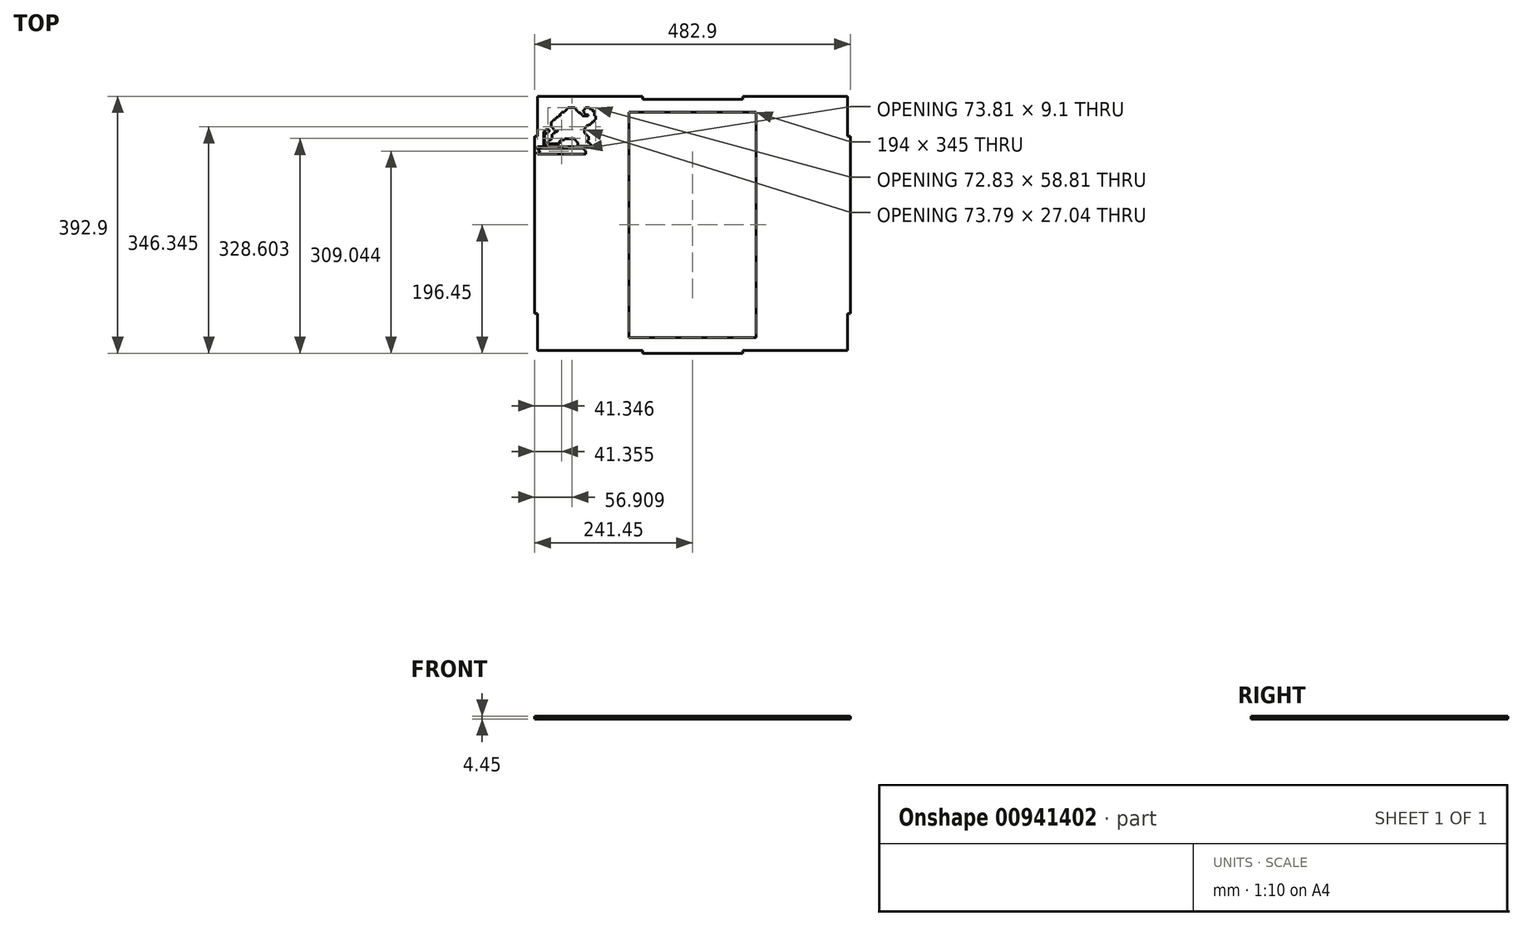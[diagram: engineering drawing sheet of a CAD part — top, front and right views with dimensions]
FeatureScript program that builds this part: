
annotation { "Feature Type Name" : "Feature", "Feature Type Description" : "" }
export const myFeature = defineFeature(function(context is Context, id is Id, definition is map)
    precondition{}
    {
        {
            var Q0;
            Q0=qCreatedBy(makeId("Top.planeOp"),FACE);
            var sketch = newSketch(context, id + "F0", { "sketchPlane" : qUnion([Q0])});
            skLineSegment(sketch, "E0.bottom", {"start": v(97, -172.5) * mm, "end": v(-97, -172.5) * mm});
            skLineSegment(sketch, "E0.top", {"start": v(97, 172.5) * mm, "end": v(-97, 172.5) * mm});
            skLineSegment(sketch, "E0.left", {"start": v(97, -172.5) * mm, "end": v(97, 172.5) * mm});
            skLineSegment(sketch, "E0.right", {"start": v(-97, -172.5) * mm, "end": v(-97, 172.5) * mm});
            skPoint(sketch, "E0.middle", {"position": v(0, 0) * mm});
            skLineSegment(sketch, "E1.bottom", {"start": v(237, -192) * mm, "end": v(76.58, -192) * mm});
            skLineSegment(sketch, "E1.top", {"start": v(76.58, 192) * mm, "end": v(-76.58, 192) * mm});
            skLineSegment(sketch, "E1.left", {"start": v(237, -192) * mm, "end": v(237, -135.76) * mm});
            skLineSegment(sketch, "E1.right", {"start": v(-237, -192) * mm, "end": v(-237, -135.76) * mm});
            skLineSegment(sketch, "E2.top", {"start": v(-237, 196.45) * mm, "end": v(-76.58, 196.45) * mm});
            skLineSegment(sketch, "E2.left", {"start": v(-237, 192) * mm, "end": v(-237, 196.45) * mm});
            skLineSegment(sketch, "E2.right", {"start": v(-76.58, 192) * mm, "end": v(-76.58, 196.45) * mm});
            skLineSegment(sketch, "E3.MirrorCS", {"start": v(76.58, 192) * mm, "end": v(76.58, 196.45) * mm});
            skLineSegment(sketch, "E4.MirrorCS", {"start": v(237, 196.45) * mm, "end": v(76.58, 196.45) * mm});
            skLineSegment(sketch, "E5.MirrorCS", {"start": v(237, 192) * mm, "end": v(237, 196.45) * mm});
            skLineSegment(sketch, "E6.top", {"start": v(-76.58, -196.45) * mm, "end": v(76.58, -196.45) * mm});
            skLineSegment(sketch, "E6.left", {"start": v(-76.58, -192) * mm, "end": v(-76.58, -196.45) * mm});
            skLineSegment(sketch, "E6.right", {"start": v(76.58, -192) * mm, "end": v(76.58, -196.45) * mm});
            skLineSegment(sketch, "E7.trimOffspring", {"start": v(-76.58, -192) * mm, "end": v(-237, -192) * mm});
            skLineSegment(sketch, "E8.bottom", {"start": v(241.45, -135.76) * mm, "end": v(237, -135.76) * mm});
            skLineSegment(sketch, "E8.top", {"start": v(241.45, 135.76) * mm, "end": v(237, 135.76) * mm});
            skLineSegment(sketch, "E8.left", {"start": v(241.45, -135.76) * mm, "end": v(241.45, 135.76) * mm});
            skLineSegment(sketch, "E8.right", {"start": v(-241.45, -135.76) * mm, "end": v(-241.45, 135.76) * mm});
            skLineSegment(sketch, "E9.trimOffspring", {"start": v(-237, 135.76) * mm, "end": v(-241.45, 135.76) * mm});
            skLineSegment(sketch, "E10.trimOffspring", {"start": v(-237, -135.76) * mm, "end": v(-241.45, -135.76) * mm});
            skLineSegment(sketch, "E11.trimOffspring", {"start": v(-237, 135.76) * mm, "end": v(-237, 192) * mm});
            skLineSegment(sketch, "E12.trimOffspring", {"start": v(237, 135.76) * mm, "end": v(237, 192) * mm});
            skLineSegment(sketch, "E13", {"start": v(-234.26, 117.12) * mm, "end": v(-234.26, 115.6) * mm});
            skLineSegment(sketch, "E14", {"start": v(-234.26, 115.6) * mm, "end": v(-232.83, 115.6) * mm});
            skLineSegment(sketch, "E15", {"start": v(-232.83, 115.6) * mm, "end": v(-232.83, 114.12) * mm});
            skLineSegment(sketch, "E16", {"start": v(-232.83, 114.12) * mm, "end": v(-231.4, 114.12) * mm});
            skLineSegment(sketch, "E17", {"start": v(-231.4, 114.12) * mm, "end": v(-231.4, 112.74) * mm});
            skLineSegment(sketch, "E18", {"start": v(-231.4, 112.74) * mm, "end": v(-230.13, 112.74) * mm});
            skLineSegment(sketch, "E19", {"start": v(-230.13, 112.74) * mm, "end": v(-230.13, 114.17) * mm});
            skLineSegment(sketch, "E20", {"start": v(-230.13, 114.17) * mm, "end": v(-228.66, 114.17) * mm});
            skLineSegment(sketch, "E21", {"start": v(-228.66, 114.17) * mm, "end": v(-228.66, 115.71) * mm});
            skLineSegment(sketch, "E22", {"start": v(-228.66, 115.71) * mm, "end": v(-227.2, 115.71) * mm});
            skLineSegment(sketch, "E23", {"start": v(-227.2, 115.71) * mm, "end": v(-227.2, 117.12) * mm});
            skLineSegment(sketch, "E24", {"start": v(-227.2, 117.12) * mm, "end": v(-222.93, 117.12) * mm});
            skLineSegment(sketch, "E25", {"start": v(-222.93, 117.12) * mm, "end": v(-222.93, 115.71) * mm});
            skLineSegment(sketch, "E26", {"start": v(-222.93, 115.71) * mm, "end": v(-221.5, 115.71) * mm});
            skLineSegment(sketch, "E27", {"start": v(-221.5, 115.71) * mm, "end": v(-221.5, 114.06) * mm});
            skLineSegment(sketch, "E28", {"start": v(-221.5, 114.06) * mm, "end": v(-220.04, 114.06) * mm});
            skLineSegment(sketch, "E29", {"start": v(-220.04, 114.06) * mm, "end": v(-220.04, 112.71) * mm});
            skLineSegment(sketch, "E30", {"start": v(-220.04, 112.71) * mm, "end": v(-218.69, 112.71) * mm});
            skLineSegment(sketch, "E31", {"start": v(-218.69, 112.71) * mm, "end": v(-218.69, 114.06) * mm});
            skLineSegment(sketch, "E32", {"start": v(-218.69, 114.06) * mm, "end": v(-217.28, 114.06) * mm});
            skLineSegment(sketch, "E33", {"start": v(-217.28, 114.06) * mm, "end": v(-217.28, 115.58) * mm});
            skLineSegment(sketch, "E34", {"start": v(-217.28, 115.58) * mm, "end": v(-215.87, 115.58) * mm});
            skLineSegment(sketch, "E35", {"start": v(-215.87, 115.58) * mm, "end": v(-215.87, 117.15) * mm});
            skLineSegment(sketch, "E36", {"start": v(-215.87, 117.15) * mm, "end": v(-211.57, 117.15) * mm});
            skLineSegment(sketch, "E37", {"start": v(-211.57, 117.15) * mm, "end": v(-211.57, 115.69) * mm});
            skLineSegment(sketch, "E38", {"start": v(-211.57, 115.69) * mm, "end": v(-210.14, 115.69) * mm});
            skLineSegment(sketch, "E39", {"start": v(-210.14, 115.69) * mm, "end": v(-210.14, 114.06) * mm});
            skLineSegment(sketch, "E40", {"start": v(-210.14, 114.06) * mm, "end": v(-208.7, 114.06) * mm});
            skLineSegment(sketch, "E41", {"start": v(-208.7, 114.06) * mm, "end": v(-208.7, 112.71) * mm});
            skLineSegment(sketch, "E42", {"start": v(-208.7, 112.71) * mm, "end": v(-207.82, 112.71) * mm});
            skLineSegment(sketch, "E43", {"start": v(-207.82, 112.71) * mm, "end": v(-207.82, 114.06) * mm});
            skLineSegment(sketch, "E44", {"start": v(-207.82, 114.06) * mm, "end": v(-206.65, 114.06) * mm});
            skLineSegment(sketch, "E45", {"start": v(-206.65, 114.06) * mm, "end": v(-206.65, 115.58) * mm});
            skLineSegment(sketch, "E46", {"start": v(-206.65, 115.58) * mm, "end": v(-205.3, 115.58) * mm});
            skLineSegment(sketch, "E47", {"start": v(-205.3, 115.58) * mm, "end": v(-205.3, 117.1) * mm});
            skLineSegment(sketch, "E48", {"start": v(-234.26, 117.12) * mm, "end": v(-237, 117.12) * mm});
            skLineSegment(sketch, "E49", {"start": v(-237, 117.12) * mm, "end": v(-237, 115.63) * mm});
            skLineSegment(sketch, "E50", {"start": v(-237, 115.63) * mm, "end": v(-235.7, 115.63) * mm});
            skLineSegment(sketch, "E51", {"start": v(-235.7, 115.63) * mm, "end": v(-235.7, 114.12) * mm});
            skLineSegment(sketch, "E52", {"start": v(-235.7, 114.12) * mm, "end": v(-234.26, 114.12) * mm});
            skLineSegment(sketch, "E53", {"start": v(-234.26, 114.12) * mm, "end": v(-234.26, 112.6) * mm});
            skLineSegment(sketch, "E54", {"start": v(-234.26, 112.6) * mm, "end": v(-232.86, 112.6) * mm});
            skLineSegment(sketch, "E55", {"start": v(-232.86, 112.6) * mm, "end": v(-232.86, 111.09) * mm});
            skLineSegment(sketch, "E56", {"start": v(-232.86, 111.09) * mm, "end": v(-237, 111.09) * mm});
            skLineSegment(sketch, "E57", {"start": v(-237, 111.09) * mm, "end": v(-237, 109.63) * mm});
            skLineSegment(sketch, "E58", {"start": v(-237, 109.63) * mm, "end": v(-163.2, 109.63) * mm});
            skLineSegment(sketch, "E59", {"start": v(-163.2, 109.63) * mm, "end": v(-163.2, 112.67) * mm});
            skLineSegment(sketch, "E60", {"start": v(-163.2, 112.67) * mm, "end": v(-163.98, 112.67) * mm});
            skLineSegment(sketch, "E61", {"start": v(-163.98, 112.67) * mm, "end": v(-163.98, 114.08) * mm});
            skLineSegment(sketch, "E62", {"start": v(-163.98, 114.08) * mm, "end": v(-165.32, 114.08) * mm});
            skLineSegment(sketch, "E63", {"start": v(-165.32, 114.08) * mm, "end": v(-165.32, 115.6) * mm});
            skLineSegment(sketch, "E64", {"start": v(-165.32, 115.6) * mm, "end": v(-166.82, 115.6) * mm});
            skLineSegment(sketch, "E65", {"start": v(-166.82, 115.6) * mm, "end": v(-166.82, 117.12) * mm});
            skLineSegment(sketch, "E66", {"start": v(-166.82, 117.12) * mm, "end": v(-171.1, 117.12) * mm});
            skLineSegment(sketch, "E67", {"start": v(-171.1, 117.12) * mm, "end": v(-171.1, 115.6) * mm});
            skLineSegment(sketch, "E68", {"start": v(-171.1, 115.6) * mm, "end": v(-172.46, 115.6) * mm});
            skLineSegment(sketch, "E69", {"start": v(-172.46, 115.6) * mm, "end": v(-172.46, 114.06) * mm});
            skLineSegment(sketch, "E70", {"start": v(-172.46, 114.06) * mm, "end": v(-173.99, 114.06) * mm});
            skLineSegment(sketch, "E71", {"start": v(-173.99, 114.06) * mm, "end": v(-173.99, 112.67) * mm});
            skLineSegment(sketch, "E72.bottom", {"start": v(-205.3, 117.1) * mm, "end": v(-200.98, 117.1) * mm});
            skLineSegment(sketch, "E72.top", {"start": v(-203.8, 115.63) * mm, "end": v(-202.3, 115.63) * mm});
            skLineSegment(sketch, "E72.left", {"start": v(-205.3, 117.1) * mm, "end": v(-205.3, 115.63) * mm});
            skLineSegment(sketch, "E72.right", {"start": v(-200.98, 117.1) * mm, "end": v(-200.98, 115.63) * mm});
            skLineSegment(sketch, "E73.bottom", {"start": v(-200.98, 115.63) * mm, "end": v(-199.6, 115.63) * mm});
            skLineSegment(sketch, "E73.top", {"start": v(-202.3, 114.04) * mm, "end": v(-200.95, 114.04) * mm});
            skLineSegment(sketch, "E73.left", {"start": v(-202.3, 115.63) * mm, "end": v(-202.3, 114.04) * mm});
            skLineSegment(sketch, "E73.right", {"start": v(-199.6, 115.63) * mm, "end": v(-199.6, 114.04) * mm});
            skLineSegment(sketch, "E74.bottom", {"start": v(-199.6, 114.04) * mm, "end": v(-198.16, 114.04) * mm});
            skLineSegment(sketch, "E74.top", {"start": v(-200.95, 112.74) * mm, "end": v(-199.55, 112.74) * mm});
            skLineSegment(sketch, "E74.left", {"start": v(-200.95, 114.04) * mm, "end": v(-200.95, 112.74) * mm});
            skLineSegment(sketch, "E74.right", {"start": v(-198.16, 114.04) * mm, "end": v(-198.16, 112.74) * mm});
            skLineSegment(sketch, "E75.bottom", {"start": v(-198.16, 112.74) * mm, "end": v(-196.75, 112.74) * mm});
            skLineSegment(sketch, "E75.left", {"start": v(-199.55, 112.74) * mm, "end": v(-199.55, 111.08) * mm});
            skLineSegment(sketch, "E75.right", {"start": v(-195.3, 112.74) * mm, "end": v(-195.3, 111.08) * mm});
            skLineSegment(sketch, "E76.bottom", {"start": v(-196.75, 114.1) * mm, "end": v(-195.3, 114.1) * mm});
            skLineSegment(sketch, "E76.top", {"start": v(-195.3, 112.74) * mm, "end": v(-193.95, 112.74) * mm});
            skLineSegment(sketch, "E76.left", {"start": v(-196.75, 114.1) * mm, "end": v(-196.75, 112.74) * mm});
            skLineSegment(sketch, "E76.right", {"start": v(-193.95, 114.1) * mm, "end": v(-193.95, 112.74) * mm});
            skLineSegment(sketch, "E77.top", {"start": v(-193.95, 114.1) * mm, "end": v(-192.4, 114.1) * mm});
            skLineSegment(sketch, "E77.left", {"start": v(-195.3, 115.58) * mm, "end": v(-195.3, 114.1) * mm});
            skLineSegment(sketch, "E77.right", {"start": v(-192.4, 115.58) * mm, "end": v(-192.4, 114.1) * mm});
            skLineSegment(sketch, "E78.bottom", {"start": v(-193.94, 117.1) * mm, "end": v(-189.56, 117.1) * mm});
            skLineSegment(sketch, "E78.left", {"start": v(-193.94, 117.1) * mm, "end": v(-193.94, 115.58) * mm});
            skLineSegment(sketch, "E78.right", {"start": v(-189.56, 117.1) * mm, "end": v(-189.56, 115.58) * mm});
            skLineSegment(sketch, "E79", {"start": v(-203.8, 115.63) * mm, "end": v(-203.8, 114.15) * mm});
            skLineSegment(sketch, "E80", {"start": v(-203.8, 114.15) * mm, "end": v(-205.27, 114.15) * mm});
            skLineSegment(sketch, "E81", {"start": v(-205.27, 114.15) * mm, "end": v(-205.27, 112.63) * mm});
            skLineSegment(sketch, "E82", {"start": v(-205.27, 112.63) * mm, "end": v(-206.61, 112.63) * mm});
            skLineSegment(sketch, "E83", {"start": v(-206.61, 112.63) * mm, "end": v(-206.61, 111.15) * mm});
            skLineSegment(sketch, "E84", {"start": v(-206.61, 111.15) * mm, "end": v(-199.55, 111.08) * mm});
            skLineSegment(sketch, "E85.bottom", {"start": v(-189.56, 115.58) * mm, "end": v(-188.16, 115.58) * mm});
            skLineSegment(sketch, "E85.top", {"start": v(-191.02, 114.05) * mm, "end": v(-189.6, 114.05) * mm});
            skLineSegment(sketch, "E85.left", {"start": v(-191.02, 115.58) * mm, "end": v(-191.02, 114.05) * mm});
            skLineSegment(sketch, "E85.right", {"start": v(-188.16, 115.58) * mm, "end": v(-188.16, 114.05) * mm});
            skLineSegment(sketch, "E86.bottom", {"start": v(-188.16, 114.05) * mm, "end": v(-186.74, 114.05) * mm});
            skLineSegment(sketch, "E86.top", {"start": v(-189.6, 112.64) * mm, "end": v(-188.16, 112.64) * mm});
            skLineSegment(sketch, "E86.left", {"start": v(-189.6, 114.05) * mm, "end": v(-189.6, 112.64) * mm});
            skLineSegment(sketch, "E86.right", {"start": v(-186.74, 114.05) * mm, "end": v(-186.74, 112.64) * mm});
            skLineSegment(sketch, "E87.bottom", {"start": v(-186.74, 112.64) * mm, "end": v(-185.4, 112.64) * mm});
            skLineSegment(sketch, "E87.left", {"start": v(-188.16, 112.64) * mm, "end": v(-188.16, 111.08) * mm});
            skLineSegment(sketch, "E87.right", {"start": v(-183.94, 112.64) * mm, "end": v(-183.94, 111.08) * mm});
            skLineSegment(sketch, "E88", {"start": v(-195.3, 111.08) * mm, "end": v(-188.16, 111.08) * mm});
            skLineSegment(sketch, "E89", {"start": v(-183.94, 112.64) * mm, "end": v(-182.48, 112.64) * mm});
            skLineSegment(sketch, "E90", {"start": v(-182.48, 112.64) * mm, "end": v(-182.48, 114.04) * mm});
            skLineSegment(sketch, "E91", {"start": v(-182.48, 114.04) * mm, "end": v(-181.05, 114.04) * mm});
            skLineSegment(sketch, "E92", {"start": v(-181.05, 114.04) * mm, "end": v(-181.05, 115.56) * mm});
            skLineSegment(sketch, "E93", {"start": v(-181.05, 115.56) * mm, "end": v(-179.73, 115.56) * mm});
            skLineSegment(sketch, "E94", {"start": v(-179.73, 115.56) * mm, "end": v(-179.73, 114.04) * mm});
            skLineSegment(sketch, "E95", {"start": v(-179.73, 114.04) * mm, "end": v(-178.33, 114.04) * mm});
            skLineSegment(sketch, "E96", {"start": v(-178.33, 114.04) * mm, "end": v(-178.33, 112.64) * mm});
            skLineSegment(sketch, "E97", {"start": v(-178.33, 112.64) * mm, "end": v(-176.86, 112.64) * mm});
            skLineSegment(sketch, "E98", {"start": v(-176.86, 112.64) * mm, "end": v(-176.86, 111.08) * mm});
            skLineSegment(sketch, "E99", {"start": v(-176.86, 111.08) * mm, "end": v(-183.94, 111.08) * mm});
            skLineSegment(sketch, "E100.right", {"start": v(-172.5, 112.64) * mm, "end": v(-172.5, 111.08) * mm});
            skLineSegment(sketch, "E101", {"start": v(-172.5, 112.64) * mm, "end": v(-171.04, 112.64) * mm});
            skLineSegment(sketch, "E102", {"start": v(-171.04, 112.64) * mm, "end": v(-171.04, 114.04) * mm});
            skLineSegment(sketch, "E103", {"start": v(-171.04, 114.04) * mm, "end": v(-169.6, 114.04) * mm});
            skLineSegment(sketch, "E104", {"start": v(-169.6, 114.04) * mm, "end": v(-169.6, 115.56) * mm});
            skLineSegment(sketch, "E105", {"start": v(-169.6, 115.56) * mm, "end": v(-168.29, 115.56) * mm});
            skLineSegment(sketch, "E106", {"start": v(-168.29, 115.56) * mm, "end": v(-168.29, 114.04) * mm});
            skLineSegment(sketch, "E107", {"start": v(-168.29, 114.04) * mm, "end": v(-166.9, 114.04) * mm});
            skLineSegment(sketch, "E108", {"start": v(-166.9, 114.04) * mm, "end": v(-166.9, 112.64) * mm});
            skLineSegment(sketch, "E109", {"start": v(-166.9, 112.64) * mm, "end": v(-165.41, 112.64) * mm});
            skLineSegment(sketch, "E110", {"start": v(-165.41, 112.64) * mm, "end": v(-165.41, 111.08) * mm});
            skLineSegment(sketch, "E111", {"start": v(-165.41, 111.08) * mm, "end": v(-172.5, 111.08) * mm});
            skLineSegment(sketch, "E112", {"start": v(-185.4, 112.64) * mm, "end": v(-185.4, 113.98) * mm});
            skLineSegment(sketch, "E113", {"start": v(-185.4, 113.98) * mm, "end": v(-185.4, 114.05) * mm});
            skLineSegment(sketch, "E114", {"start": v(-185.4, 114.05) * mm, "end": v(-183.97, 114.05) * mm});
            skLineSegment(sketch, "E115", {"start": v(-183.97, 114.05) * mm, "end": v(-183.97, 115.58) * mm});
            skLineSegment(sketch, "E116", {"start": v(-183.97, 115.58) * mm, "end": v(-182.53, 115.58) * mm});
            skLineSegment(sketch, "E117", {"start": v(-182.53, 115.58) * mm, "end": v(-182.53, 117.13) * mm});
            skLineSegment(sketch, "E118", {"start": v(-182.53, 117.13) * mm, "end": v(-178.25, 117.13) * mm});
            skLineSegment(sketch, "E119", {"start": v(-178.25, 117.13) * mm, "end": v(-178.25, 115.68) * mm});
            skLineSegment(sketch, "E120", {"start": v(-178.25, 115.68) * mm, "end": v(-176.8, 115.68) * mm});
            skLineSegment(sketch, "E121", {"start": v(-176.8, 115.68) * mm, "end": v(-176.8, 114.05) * mm});
            skLineSegment(sketch, "E122", {"start": v(-176.8, 114.05) * mm, "end": v(-175.35, 114.05) * mm});
            skLineSegment(sketch, "E123", {"start": v(-175.35, 114.05) * mm, "end": v(-175.35, 112.67) * mm});
            skLineSegment(sketch, "E124", {"start": v(-175.35, 112.67) * mm, "end": v(-173.99, 112.67) * mm});
            skLineSegment(sketch, "E125", {"start": v(-192.4, 115.58) * mm, "end": v(-191.02, 115.58) * mm});
            skLineSegment(sketch, "E126.top", {"start": v(-214.47, 115.57) * mm, "end": v(-212.97, 115.57) * mm});
            skLineSegment(sketch, "E127.top", {"start": v(-212.97, 113.98) * mm, "end": v(-211.61, 113.98) * mm});
            skLineSegment(sketch, "E127.left", {"start": v(-212.97, 115.57) * mm, "end": v(-212.97, 113.98) * mm});
            skLineSegment(sketch, "E128.top", {"start": v(-211.61, 112.68) * mm, "end": v(-210.22, 112.68) * mm});
            skLineSegment(sketch, "E128.left", {"start": v(-211.61, 113.98) * mm, "end": v(-211.61, 112.68) * mm});
            skLineSegment(sketch, "E129.left", {"start": v(-210.22, 112.68) * mm, "end": v(-210.22, 111.02) * mm});
            skLineSegment(sketch, "E130", {"start": v(-214.47, 115.57) * mm, "end": v(-214.47, 114.09) * mm});
            skLineSegment(sketch, "E131", {"start": v(-214.47, 114.09) * mm, "end": v(-215.86, 114.09) * mm});
            skLineSegment(sketch, "E132", {"start": v(-215.86, 114.09) * mm, "end": v(-215.86, 112.62) * mm});
            skLineSegment(sketch, "E133", {"start": v(-215.86, 112.62) * mm, "end": v(-217.28, 112.62) * mm});
            skLineSegment(sketch, "E134", {"start": v(-217.28, 111.09) * mm, "end": v(-210.22, 111.02) * mm});
            skLineSegment(sketch, "E135", {"start": v(-217.28, 112.62) * mm, "end": v(-217.28, 111.09) * mm});
            skLineSegment(sketch, "E136.top", {"start": v(-225.72, 115.6) * mm, "end": v(-224.32, 115.6) * mm});
            skLineSegment(sketch, "E137.top", {"start": v(-224.32, 114.03) * mm, "end": v(-222.94, 114.03) * mm});
            skLineSegment(sketch, "E137.left", {"start": v(-224.32, 115.6) * mm, "end": v(-224.32, 114.03) * mm});
            skLineSegment(sketch, "E138.top", {"start": v(-222.94, 112.62) * mm, "end": v(-221.48, 112.62) * mm});
            skLineSegment(sketch, "E138.left", {"start": v(-222.94, 114.03) * mm, "end": v(-222.94, 112.62) * mm});
            skLineSegment(sketch, "E139.left", {"start": v(-221.48, 112.62) * mm, "end": v(-221.48, 111.05) * mm});
            skLineSegment(sketch, "E140", {"start": v(-225.72, 115.6) * mm, "end": v(-225.72, 114.03) * mm});
            skLineSegment(sketch, "E141", {"start": v(-225.72, 114.03) * mm, "end": v(-227.13, 114.03) * mm});
            skLineSegment(sketch, "E142", {"start": v(-227.13, 114.03) * mm, "end": v(-227.13, 112.65) * mm});
            skLineSegment(sketch, "E143", {"start": v(-227.13, 112.65) * mm, "end": v(-228.54, 112.65) * mm});
            skLineSegment(sketch, "E144", {"start": v(-228.54, 111.12) * mm, "end": v(-221.48, 111.05) * mm});
            skLineSegment(sketch, "E145", {"start": v(-228.54, 112.65) * mm, "end": v(-228.54, 111.12) * mm});
            skLineSegment(sketch, "E146", {"start": v(-237, 118.63) * mm, "end": v(-163.2, 118.63) * mm});
            skLineSegment(sketch, "E147", {"start": v(-163.2, 118.63) * mm, "end": v(-163.2, 117.12) * mm});
            skLineSegment(sketch, "E148", {"start": v(-163.2, 117.12) * mm, "end": v(-237, 117.12) * mm});
            skLineSegment(sketch, "E149", {"start": v(-163.2, 118.63) * mm, "end": v(-163.2, 119.95) * mm});
            skLineSegment(sketch, "E150", {"start": v(-163.2, 119.95) * mm, "end": v(-237, 119.95) * mm});
            skLineSegment(sketch, "E151", {"start": v(-237, 119.95) * mm, "end": v(-237, 118.63) * mm});
            skLineSegment(sketch, "E152", {"start": v(-163.2, 109.63) * mm, "end": v(-163.19, 108.04) * mm});
            skLineSegment(sketch, "E153", {"start": v(-163.19, 108.04) * mm, "end": v(-237, 108.04) * mm});
            skLineSegment(sketch, "E154", {"start": v(-237, 108.04) * mm, "end": v(-237, 109.63) * mm});
            skLineSegment(sketch, "E155", {"start": v(-227.44, 119.95) * mm, "end": v(-227.44, 142.75) * mm});
            skLineSegment(sketch, "E156", {"start": v(-227.44, 142.75) * mm, "end": v(-226.03, 142.75) * mm});
            skLineSegment(sketch, "E157", {"start": v(-226.03, 142.75) * mm, "end": v(-226.03, 144.1) * mm});
            skLineSegment(sketch, "E158", {"start": v(-226.03, 144.1) * mm, "end": v(-224.61, 144.1) * mm});
            skLineSegment(sketch, "E159", {"start": v(-224.61, 144.1) * mm, "end": v(-224.61, 145.67) * mm});
            skLineSegment(sketch, "E160", {"start": v(-224.61, 145.67) * mm, "end": v(-218.88, 145.67) * mm});
            skLineSegment(sketch, "E161", {"start": v(-218.88, 145.67) * mm, "end": v(-218.88, 142.65) * mm});
            skLineSegment(sketch, "E162", {"start": v(-218.88, 142.65) * mm, "end": v(-220.26, 142.65) * mm});
            skLineSegment(sketch, "E163", {"start": v(-220.26, 142.65) * mm, "end": v(-220.26, 141.4) * mm});
            skLineSegment(sketch, "E164", {"start": v(-220.26, 141.4) * mm, "end": v(-221.7, 141.4) * mm});
            skLineSegment(sketch, "E165", {"start": v(-221.7, 141.4) * mm, "end": v(-221.7, 139.73) * mm});
            skLineSegment(sketch, "E166", {"start": v(-221.7, 139.73) * mm, "end": v(-225.9, 139.73) * mm});
            skLineSegment(sketch, "E167", {"start": v(-225.9, 139.73) * mm, "end": v(-225.9, 122.94) * mm});
            skLineSegment(sketch, "E168", {"start": v(-225.9, 122.94) * mm, "end": v(-224.61, 122.94) * mm});
            skLineSegment(sketch, "E169", {"start": v(-224.61, 122.94) * mm, "end": v(-224.61, 121.47) * mm});
            skLineSegment(sketch, "E170", {"start": v(-224.61, 121.47) * mm, "end": v(-223.26, 121.47) * mm});
            skLineSegment(sketch, "E171", {"start": v(-223.26, 121.47) * mm, "end": v(-223.26, 119.95) * mm});
            skLineSegment(sketch, "E172", {"start": v(-220.88, 124.17) * mm, "end": v(-203.52, 124.17) * mm});
            skLineSegment(sketch, "E173", {"start": v(-203.52, 124.17) * mm, "end": v(-203.52, 127.8) * mm});
            skLineSegment(sketch, "E174", {"start": v(-203.52, 127.8) * mm, "end": v(-201.8, 127.8) * mm});
            skLineSegment(sketch, "E175", {"start": v(-201.8, 127.8) * mm, "end": v(-201.8, 129.63) * mm});
            skLineSegment(sketch, "E176", {"start": v(-201.8, 129.63) * mm, "end": v(-195.46, 129.63) * mm});
            skLineSegment(sketch, "E177", {"start": v(-195.46, 129.63) * mm, "end": v(-195.46, 131.47) * mm});
            skLineSegment(sketch, "E178", {"start": v(-195.46, 131.47) * mm, "end": v(-179.83, 131.47) * mm});
            skLineSegment(sketch, "E179", {"start": v(-179.83, 131.47) * mm, "end": v(-179.83, 129.7) * mm});
            skLineSegment(sketch, "E180", {"start": v(-179.83, 129.7) * mm, "end": v(-178.26, 129.7) * mm});
            skLineSegment(sketch, "E181", {"start": v(-178.26, 129.7) * mm, "end": v(-178.26, 127.69) * mm});
            skLineSegment(sketch, "E182", {"start": v(-178.26, 127.69) * mm, "end": v(-176.64, 127.69) * mm});
            skLineSegment(sketch, "E183", {"start": v(-176.64, 127.69) * mm, "end": v(-176.64, 125.9) * mm});
            skLineSegment(sketch, "E184", {"start": v(-176.64, 125.9) * mm, "end": v(-175.07, 125.9) * mm});
            skLineSegment(sketch, "E185", {"start": v(-175.07, 125.9) * mm, "end": v(-175.07, 122.33) * mm});
            skLineSegment(sketch, "E186", {"start": v(-175.07, 122.33) * mm, "end": v(-173.45, 122.33) * mm});
            skLineSegment(sketch, "E187", {"start": v(-173.45, 122.33) * mm, "end": v(-173.45, 120.5) * mm});
            skLineSegment(sketch, "E188", {"start": v(-173.45, 120.5) * mm, "end": v(-154.41, 120.5) * mm});
            skLineSegment(sketch, "E189", {"start": v(-154.41, 120.5) * mm, "end": v(-154.41, 122.28) * mm});
            skLineSegment(sketch, "E190", {"start": v(-154.41, 122.28) * mm, "end": v(-155.93, 122.28) * mm});
            skLineSegment(sketch, "E191", {"start": v(-155.93, 122.28) * mm, "end": v(-155.93, 124.28) * mm});
            skLineSegment(sketch, "E192", {"start": v(-155.93, 124.28) * mm, "end": v(-157.55, 124.28) * mm});
            skLineSegment(sketch, "E193", {"start": v(-157.55, 124.28) * mm, "end": v(-157.55, 126) * mm});
            skLineSegment(sketch, "E194", {"start": v(-157.55, 126) * mm, "end": v(-160.69, 126) * mm});
            skLineSegment(sketch, "E195", {"start": v(-160.69, 126) * mm, "end": v(-160.69, 129.58) * mm});
            skLineSegment(sketch, "E196", {"start": v(-160.69, 129.58) * mm, "end": v(-159.01, 129.58) * mm});
            skLineSegment(sketch, "E197", {"start": v(-159.01, 129.58) * mm, "end": v(-159.01, 135.26) * mm});
            skLineSegment(sketch, "E198", {"start": v(-159.01, 135.26) * mm, "end": v(-160.85, 135.26) * mm});
            skLineSegment(sketch, "E199", {"start": v(-160.85, 135.26) * mm, "end": v(-160.85, 137.1) * mm});
            skLineSegment(sketch, "E200", {"start": v(-160.85, 137.1) * mm, "end": v(-162.42, 137.1) * mm});
            skLineSegment(sketch, "E201", {"start": v(-162.42, 137.1) * mm, "end": v(-162.42, 138.9) * mm});
            skLineSegment(sketch, "E202", {"start": v(-162.42, 138.9) * mm, "end": v(-163.93, 138.9) * mm});
            skLineSegment(sketch, "E203", {"start": v(-163.93, 138.9) * mm, "end": v(-163.93, 140.88) * mm});
            skLineSegment(sketch, "E204", {"start": v(-163.93, 140.88) * mm, "end": v(-165.45, 140.88) * mm});
            skLineSegment(sketch, "E205", {"start": v(-165.45, 140.88) * mm, "end": v(-165.45, 147.86) * mm});
            skLineSegment(sketch, "E206", {"start": v(-165.45, 147.86) * mm, "end": v(-163.93, 147.86) * mm});
            skLineSegment(sketch, "E207", {"start": v(-163.93, 147.86) * mm, "end": v(-163.93, 149.7) * mm});
            skLineSegment(sketch, "E208", {"start": v(-163.93, 149.7) * mm, "end": v(-162.2, 149.7) * mm});
            skLineSegment(sketch, "E209", {"start": v(-162.2, 149.7) * mm, "end": v(-162.2, 151.7) * mm});
            skLineSegment(sketch, "E210", {"start": v(-162.2, 151.7) * mm, "end": v(-158.9, 151.7) * mm});
            skLineSegment(sketch, "E211", {"start": v(-158.9, 151.7) * mm, "end": v(-158.9, 153.53) * mm});
            skLineSegment(sketch, "E212", {"start": v(-158.9, 153.53) * mm, "end": v(-155.95, 153.53) * mm});
            skLineSegment(sketch, "E213", {"start": v(-155.95, 153.53) * mm, "end": v(-155.95, 155.38) * mm});
            skLineSegment(sketch, "E214", {"start": v(-155.95, 155.38) * mm, "end": v(-154.43, 155.38) * mm});
            skLineSegment(sketch, "E215", {"start": v(-154.43, 155.38) * mm, "end": v(-154.43, 157.02) * mm});
            skLineSegment(sketch, "E216", {"start": v(-154.43, 157.02) * mm, "end": v(-151.35, 157.02) * mm});
            skLineSegment(sketch, "E217", {"start": v(-151.35, 157.02) * mm, "end": v(-151.35, 159) * mm});
            skLineSegment(sketch, "E218", {"start": v(-151.35, 159) * mm, "end": v(-149.83, 159) * mm});
            skLineSegment(sketch, "E219", {"start": v(-149.83, 159) * mm, "end": v(-149.83, 160.82) * mm});
            skLineSegment(sketch, "E220", {"start": v(-149.83, 160.82) * mm, "end": v(-148.13, 160.82) * mm});
            skLineSegment(sketch, "E221", {"start": v(-148.13, 160.82) * mm, "end": v(-148.13, 166.43) * mm});
            skLineSegment(sketch, "E222", {"start": v(-148.13, 166.43) * mm, "end": v(-149.83, 166.43) * mm});
            skLineSegment(sketch, "E223", {"start": v(-149.83, 166.43) * mm, "end": v(-149.83, 172.06) * mm});
            skLineSegment(sketch, "E224", {"start": v(-149.83, 172.06) * mm, "end": v(-151.23, 172.06) * mm});
            skLineSegment(sketch, "E225", {"start": v(-151.23, 172.06) * mm, "end": v(-151.23, 175.69) * mm});
            skLineSegment(sketch, "E226", {"start": v(-151.23, 175.69) * mm, "end": v(-154.43, 175.69) * mm});
            skLineSegment(sketch, "E227", {"start": v(-154.43, 175.69) * mm, "end": v(-154.43, 177.52) * mm});
            skLineSegment(sketch, "E228", {"start": v(-154.43, 177.52) * mm, "end": v(-157.64, 177.52) * mm});
            skLineSegment(sketch, "E229", {"start": v(-157.64, 177.52) * mm, "end": v(-157.64, 179.3) * mm});
            skLineSegment(sketch, "E230", {"start": v(-157.64, 179.3) * mm, "end": v(-164.01, 179.3) * mm});
            skLineSegment(sketch, "E231", {"start": v(-164.01, 179.3) * mm, "end": v(-164.01, 177.52) * mm});
            skLineSegment(sketch, "E232", {"start": v(-164.01, 177.52) * mm, "end": v(-165.45, 177.52) * mm});
            skLineSegment(sketch, "E233", {"start": v(-165.45, 177.52) * mm, "end": v(-165.45, 175.77) * mm});
            skLineSegment(sketch, "E234", {"start": v(-165.45, 175.77) * mm, "end": v(-167.1, 175.77) * mm});
            skLineSegment(sketch, "E235", {"start": v(-167.1, 175.77) * mm, "end": v(-167.1, 173.8) * mm});
            skLineSegment(sketch, "E236", {"start": v(-167.1, 173.8) * mm, "end": v(-165.6, 173.8) * mm});
            skLineSegment(sketch, "E237", {"start": v(-165.6, 173.8) * mm, "end": v(-165.6, 170.17) * mm});
            skLineSegment(sketch, "E238", {"start": v(-165.6, 170.17) * mm, "end": v(-164.04, 170.17) * mm});
            skLineSegment(sketch, "E239", {"start": v(-164.04, 170.17) * mm, "end": v(-164.04, 168.28) * mm});
            skLineSegment(sketch, "E240", {"start": v(-164.04, 168.28) * mm, "end": v(-159.26, 168.28) * mm});
            skLineSegment(sketch, "E241", {"start": v(-159.26, 168.28) * mm, "end": v(-159.26, 166.46) * mm});
            skLineSegment(sketch, "E242", {"start": v(-159.26, 166.46) * mm, "end": v(-168.69, 166.46) * mm});
            skLineSegment(sketch, "E243", {"start": v(-168.69, 166.46) * mm, "end": v(-168.69, 168.34) * mm});
            skLineSegment(sketch, "E244", {"start": v(-168.69, 168.34) * mm, "end": v(-170.05, 168.34) * mm});
            skLineSegment(sketch, "E245", {"start": v(-170.05, 168.34) * mm, "end": v(-170.05, 170.17) * mm});
            skLineSegment(sketch, "E246", {"start": v(-170.05, 170.17) * mm, "end": v(-171.82, 170.17) * mm});
            skLineSegment(sketch, "E247", {"start": v(-171.82, 170.17) * mm, "end": v(-171.82, 171.97) * mm});
            skLineSegment(sketch, "E248", {"start": v(-171.82, 171.97) * mm, "end": v(-174.95, 171.97) * mm});
            skLineSegment(sketch, "E249", {"start": v(-174.95, 171.97) * mm, "end": v(-174.95, 173.81) * mm});
            skLineSegment(sketch, "E250", {"start": v(-174.95, 173.81) * mm, "end": v(-176.61, 173.81) * mm});
            skLineSegment(sketch, "E251", {"start": v(-176.61, 173.81) * mm, "end": v(-176.61, 175.67) * mm});
            skLineSegment(sketch, "E252", {"start": v(-176.61, 175.67) * mm, "end": v(-178.08, 175.67) * mm});
            skLineSegment(sketch, "E253", {"start": v(-178.08, 175.67) * mm, "end": v(-178.08, 177.64) * mm});
            skLineSegment(sketch, "E254", {"start": v(-178.08, 177.64) * mm, "end": v(-179.65, 177.64) * mm});
            skLineSegment(sketch, "E255", {"start": v(-179.65, 177.64) * mm, "end": v(-179.65, 179.26) * mm});
            skLineSegment(sketch, "E256", {"start": v(-179.65, 179.26) * mm, "end": v(-190.68, 179.26) * mm});
            skLineSegment(sketch, "E257", {"start": v(-190.68, 179.26) * mm, "end": v(-190.68, 177.58) * mm});
            skLineSegment(sketch, "E258", {"start": v(-190.68, 177.58) * mm, "end": v(-192.33, 177.58) * mm});
            skLineSegment(sketch, "E259", {"start": v(-192.33, 177.58) * mm, "end": v(-192.33, 175.67) * mm});
            skLineSegment(sketch, "E260", {"start": v(-192.33, 175.67) * mm, "end": v(-193.82, 175.67) * mm});
            skLineSegment(sketch, "E261", {"start": v(-193.82, 175.67) * mm, "end": v(-193.82, 173.99) * mm});
            skLineSegment(sketch, "E262", {"start": v(-193.82, 173.99) * mm, "end": v(-195.52, 173.99) * mm});
            skLineSegment(sketch, "E263", {"start": v(-195.52, 173.99) * mm, "end": v(-195.52, 172.07) * mm});
            skLineSegment(sketch, "E264", {"start": v(-195.52, 172.07) * mm, "end": v(-200.36, 172.07) * mm});
            skLineSegment(sketch, "E265", {"start": v(-200.36, 172.07) * mm, "end": v(-200.36, 170.17) * mm});
            skLineSegment(sketch, "E266", {"start": v(-200.36, 170.17) * mm, "end": v(-201.87, 170.17) * mm});
            skLineSegment(sketch, "E267", {"start": v(-201.87, 170.17) * mm, "end": v(-201.87, 166.58) * mm});
            skLineSegment(sketch, "E268", {"start": v(-201.87, 166.58) * mm, "end": v(-204.98, 166.58) * mm});
            skLineSegment(sketch, "E269", {"start": v(-204.98, 166.58) * mm, "end": v(-204.98, 164.65) * mm});
            skLineSegment(sketch, "E270", {"start": v(-204.98, 164.65) * mm, "end": v(-208.22, 164.65) * mm});
            skLineSegment(sketch, "E271", {"start": v(-208.22, 164.65) * mm, "end": v(-208.22, 162.8) * mm});
            skLineSegment(sketch, "E272", {"start": v(-208.22, 162.8) * mm, "end": v(-209.87, 162.8) * mm});
            skLineSegment(sketch, "E273", {"start": v(-209.87, 162.8) * mm, "end": v(-209.87, 161.04) * mm});
            skLineSegment(sketch, "E274", {"start": v(-209.87, 161.04) * mm, "end": v(-213.02, 161.04) * mm});
            skLineSegment(sketch, "E275", {"start": v(-213.02, 161.04) * mm, "end": v(-213.02, 159.15) * mm});
            skLineSegment(sketch, "E276", {"start": v(-213.02, 159.15) * mm, "end": v(-214.62, 159.15) * mm});
            skLineSegment(sketch, "E277", {"start": v(-214.62, 159.15) * mm, "end": v(-214.62, 157.27) * mm});
            skLineSegment(sketch, "E278", {"start": v(-214.62, 157.27) * mm, "end": v(-216.22, 157.27) * mm});
            skLineSegment(sketch, "E279", {"start": v(-216.22, 157.27) * mm, "end": v(-216.22, 149.89) * mm});
            skLineSegment(sketch, "E280", {"start": v(-216.22, 149.89) * mm, "end": v(-214.46, 149.89) * mm});
            skLineSegment(sketch, "E281", {"start": v(-214.46, 149.89) * mm, "end": v(-214.46, 147.97) * mm});
            skLineSegment(sketch, "E282", {"start": v(-214.46, 147.97) * mm, "end": v(-213.02, 147.97) * mm});
            skLineSegment(sketch, "E283", {"start": v(-213.02, 147.97) * mm, "end": v(-213.02, 146.25) * mm});
            skLineSegment(sketch, "E284", {"start": v(-213.02, 146.25) * mm, "end": v(-211.34, 146.25) * mm});
            skLineSegment(sketch, "E285", {"start": v(-211.34, 146.25) * mm, "end": v(-211.34, 144.26) * mm});
            skLineSegment(sketch, "E286", {"start": v(-211.34, 144.26) * mm, "end": v(-206.44, 144.26) * mm});
            skLineSegment(sketch, "E287", {"start": v(-206.44, 144.26) * mm, "end": v(-206.44, 142.54) * mm});
            skLineSegment(sketch, "E288", {"start": v(-206.44, 142.54) * mm, "end": v(-209.92, 142.54) * mm});
            skLineSegment(sketch, "E289", {"start": v(-209.92, 142.54) * mm, "end": v(-209.92, 140.82) * mm});
            skLineSegment(sketch, "E290", {"start": v(-209.92, 140.82) * mm, "end": v(-212.98, 140.82) * mm});
            skLineSegment(sketch, "E291", {"start": v(-212.98, 140.82) * mm, "end": v(-212.98, 138.95) * mm});
            skLineSegment(sketch, "E292", {"start": v(-212.98, 138.95) * mm, "end": v(-214.55, 138.95) * mm});
            skLineSegment(sketch, "E293", {"start": v(-214.55, 138.95) * mm, "end": v(-214.55, 131.53) * mm});
            skLineSegment(sketch, "E294", {"start": v(-214.55, 131.53) * mm, "end": v(-216.22, 131.53) * mm});
            skLineSegment(sketch, "E295", {"start": v(-216.22, 131.53) * mm, "end": v(-216.22, 129.7) * mm});
            skLineSegment(sketch, "E296", {"start": v(-216.22, 129.7) * mm, "end": v(-219.35, 129.7) * mm});
            skLineSegment(sketch, "E297", {"start": v(-219.35, 129.7) * mm, "end": v(-219.35, 127.77) * mm});
            skLineSegment(sketch, "E298", {"start": v(-219.35, 127.77) * mm, "end": v(-220.95, 127.77) * mm});
            skLineSegment(sketch, "E299", {"start": v(-220.95, 127.77) * mm, "end": v(-220.88, 124.17) * mm});
            skLineSegment(sketch, "E300.bottom", {"start": v(-171.67, 149.98) * mm, "end": v(-173.57, 149.98) * mm});
            skLineSegment(sketch, "E300.top", {"start": v(-171.67, 148.03) * mm, "end": v(-173.57, 148.03) * mm});
            skLineSegment(sketch, "E300.left", {"start": v(-171.67, 149.98) * mm, "end": v(-171.67, 148.03) * mm});
            skLineSegment(sketch, "E300.right", {"start": v(-173.57, 149.98) * mm, "end": v(-173.57, 148.03) * mm});
            skLineSegment(sketch, "E301.bottom", {"start": v(-171.67, 148.03) * mm, "end": v(-170.23, 148.03) * mm});
            skLineSegment(sketch, "E301.top", {"start": v(-171.67, 146.25) * mm, "end": v(-170.23, 146.25) * mm});
            skLineSegment(sketch, "E301.left", {"start": v(-171.67, 148.03) * mm, "end": v(-171.67, 146.25) * mm});
            skLineSegment(sketch, "E301.right", {"start": v(-170.23, 148.03) * mm, "end": v(-170.23, 146.25) * mm});
            skLineSegment(sketch, "E302.bottom", {"start": v(-171.67, 146.25) * mm, "end": v(-175.03, 146.25) * mm});
            skLineSegment(sketch, "E302.top", {"start": v(-171.67, 142.68) * mm, "end": v(-175.03, 142.68) * mm});
            skLineSegment(sketch, "E302.left", {"start": v(-171.67, 146.25) * mm, "end": v(-171.67, 142.68) * mm});
            skLineSegment(sketch, "E302.right", {"start": v(-175.03, 146.25) * mm, "end": v(-175.03, 142.68) * mm});
            skLineSegment(sketch, "E303.bottom", {"start": v(-173.35, 142.68) * mm, "end": v(-175.03, 142.68) * mm});
            skLineSegment(sketch, "E303.top", {"start": v(-173.35, 140.68) * mm, "end": v(-175.03, 140.68) * mm});
            skLineSegment(sketch, "E303.left", {"start": v(-173.35, 142.68) * mm, "end": v(-173.35, 140.68) * mm});
            skLineSegment(sketch, "E303.right", {"start": v(-175.03, 142.68) * mm, "end": v(-175.03, 140.68) * mm});
            skLineSegment(sketch, "E304.bottom", {"start": v(-173.35, 140.68) * mm, "end": v(-171.67, 140.68) * mm});
            skLineSegment(sketch, "E304.top", {"start": v(-173.35, 138.84) * mm, "end": v(-171.67, 138.84) * mm});
            skLineSegment(sketch, "E304.left", {"start": v(-173.35, 140.68) * mm, "end": v(-173.35, 138.84) * mm});
            skLineSegment(sketch, "E304.right", {"start": v(-171.67, 140.68) * mm, "end": v(-171.67, 138.84) * mm});
            skLineSegment(sketch, "E305.bottom", {"start": v(-171.67, 140.68) * mm, "end": v(-170.1, 140.68) * mm});
            skLineSegment(sketch, "E305.top", {"start": v(-171.67, 142.57) * mm, "end": v(-170.1, 142.57) * mm});
            skLineSegment(sketch, "E305.left", {"start": v(-171.67, 140.68) * mm, "end": v(-171.67, 142.57) * mm});
            skLineSegment(sketch, "E305.right", {"start": v(-170.1, 140.68) * mm, "end": v(-170.1, 142.57) * mm});
            skLineSegment(sketch, "E306.bottom", {"start": v(-175.03, 146.25) * mm, "end": v(-176.63, 146.25) * mm});
            skLineSegment(sketch, "E306.top", {"start": v(-176.62, 148.06) * mm, "end": v(-176.63, 148.06) * mm});
            skLineSegment(sketch, "E306.left", {"start": v(-175.03, 146.25) * mm, "end": v(-175.03, 148.06) * mm});
            skLineSegment(sketch, "E306.right", {"start": v(-176.63, 146.25) * mm, "end": v(-176.63, 148.06) * mm});
            skLineSegment(sketch, "E307.top", {"start": v(-175.03, 149.87) * mm, "end": v(-176.62, 149.87) * mm});
            skLineSegment(sketch, "E307.left", {"start": v(-175.03, 148.06) * mm, "end": v(-175.03, 149.87) * mm});
            skLineSegment(sketch, "E308.bottom", {"start": v(-176.62, 149.87) * mm, "end": v(-178.14, 149.87) * mm});
            skLineSegment(sketch, "E308.top", {"start": v(-176.62, 148.06) * mm, "end": v(-178.14, 148.06) * mm});
            skLineSegment(sketch, "E309.bottom", {"start": v(-178.14, 149.87) * mm, "end": v(-179.76, 149.87) * mm});
            skLineSegment(sketch, "E309.top", {"start": v(-178.14, 148.06) * mm, "end": v(-179.76, 148.06) * mm});
            skLineSegment(sketch, "E310.bottom", {"start": v(-179.76, 149.87) * mm, "end": v(-181.27, 149.87) * mm});
            skLineSegment(sketch, "E310.top", {"start": v(-179.76, 148.06) * mm, "end": v(-181.27, 148.06) * mm});
            skLineSegment(sketch, "E311.bottom", {"start": v(-181.27, 149.87) * mm, "end": v(-182.92, 149.87) * mm});
            skLineSegment(sketch, "E311.top", {"start": v(-181.27, 148.06) * mm, "end": v(-182.92, 148.06) * mm});
            skLineSegment(sketch, "E312.bottom", {"start": v(-182.92, 149.87) * mm, "end": v(-184.4, 149.87) * mm});
            skLineSegment(sketch, "E312.top", {"start": v(-182.92, 148.06) * mm, "end": v(-184.4, 148.06) * mm});
            skLineSegment(sketch, "E312.right", {"start": v(-184.4, 149.87) * mm, "end": v(-184.4, 148.06) * mm});
            skLineSegment(sketch, "E313", {"start": v(-175.03, 140.68) * mm, "end": v(-182.87, 140.68) * mm});
            skLineSegment(sketch, "E314", {"start": v(-182.87, 140.68) * mm, "end": v(-182.87, 142.57) * mm});
            skLineSegment(sketch, "E315", {"start": v(-182.87, 142.57) * mm, "end": v(-184.4, 142.57) * mm});
            skLineSegment(sketch, "E316", {"start": v(-184.4, 142.57) * mm, "end": v(-184.4, 148.06) * mm});
            skLineSegment(sketch, "E317", {"start": v(-182.87, 140.68) * mm, "end": v(-184.4, 140.68) * mm});
            skLineSegment(sketch, "E318", {"start": v(-184.4, 140.68) * mm, "end": v(-184.4, 142.57) * mm});
            skLineSegment(sketch, "E319", {"start": v(-184.4, 142.57) * mm, "end": v(-187.7, 142.6) * mm});
            skLineSegment(sketch, "E320", {"start": v(-187.7, 142.6) * mm, "end": v(-187.7, 148.06) * mm});
            skLineSegment(sketch, "E321", {"start": v(-187.7, 148.06) * mm, "end": v(-184.4, 148.06) * mm});
            skLineSegment(sketch, "E322", {"start": v(-187.7, 148.06) * mm, "end": v(-187.7, 149.9) * mm});
            skLineSegment(sketch, "E323", {"start": v(-187.7, 149.9) * mm, "end": v(-192.34, 149.9) * mm});
            skLineSegment(sketch, "E324", {"start": v(-192.34, 149.9) * mm, "end": v(-192.34, 151.83) * mm});
            skLineSegment(sketch, "E325", {"start": v(-192.34, 151.83) * mm, "end": v(-197.29, 151.83) * mm});
            skLineSegment(sketch, "E326", {"start": v(-197.29, 151.83) * mm, "end": v(-197.29, 148.06) * mm});
            skLineSegment(sketch, "E327", {"start": v(-197.29, 148.06) * mm, "end": v(-195.55, 148.06) * mm});
            skLineSegment(sketch, "E328", {"start": v(-195.55, 148.06) * mm, "end": v(-195.55, 146.21) * mm});
            skLineSegment(sketch, "E329", {"start": v(-195.55, 146.21) * mm, "end": v(-192.37, 146.21) * mm});
            skLineSegment(sketch, "E330", {"start": v(-192.37, 148.06) * mm, "end": v(-192.37, 146.2) * mm});
            skLineSegment(sketch, "E331", {"start": v(-193.88, 144.37) * mm, "end": v(-195.49, 144.34) * mm});
            skLineSegment(sketch, "E332", {"start": v(-195.49, 144.34) * mm, "end": v(-195.55, 146.21) * mm});
            skLineSegment(sketch, "E333", {"start": v(-192.4, 144.35) * mm, "end": v(-192.36, 142.54) * mm});
            skLineSegment(sketch, "E334", {"start": v(-192.36, 142.54) * mm, "end": v(-193.88, 142.51) * mm});
            skLineSegment(sketch, "E335", {"start": v(-193.88, 142.51) * mm, "end": v(-193.88, 144.37) * mm});
            skLineSegment(sketch, "E336", {"start": v(-192.4, 144.35) * mm, "end": v(-193.88, 144.35) * mm});
            skLineSegment(sketch, "E337", {"start": v(-193.98, 146.21) * mm, "end": v(-193.98, 144.37) * mm});
            skPoint(sketch, "E338.start.orphan", {"position": v(-192.13, 148.06) * mm});
            skLineSegment(sketch, "E339", {"start": v(-192.37, 148.06) * mm, "end": v(-193.95, 148.06) * mm});
            skLineSegment(sketch, "E340", {"start": v(-193.95, 148.06) * mm, "end": v(-193.98, 146.21) * mm});
            skLineSegment(sketch, "E341", {"start": v(-195.49, 144.34) * mm, "end": v(-195.46, 142.7) * mm});
            skLineSegment(sketch, "E342", {"start": v(-195.46, 142.7) * mm, "end": v(-200.32, 142.7) * mm});
            skLineSegment(sketch, "E343", {"start": v(-200.32, 142.7) * mm, "end": v(-200.32, 140.71) * mm});
            skLineSegment(sketch, "E344", {"start": v(-200.32, 140.71) * mm, "end": v(-197.21, 140.71) * mm});
            skLineSegment(sketch, "E345", {"start": v(-197.21, 140.71) * mm, "end": v(-197.21, 138.78) * mm});
            skLineSegment(sketch, "E346", {"start": v(-197.21, 138.78) * mm, "end": v(-195.49, 138.78) * mm});
            skLineSegment(sketch, "E347", {"start": v(-195.49, 138.78) * mm, "end": v(-195.49, 135.23) * mm});
            skLineSegment(sketch, "E348", {"start": v(-195.49, 135.23) * mm, "end": v(-193.94, 135.23) * mm});
            skLineSegment(sketch, "E349", {"start": v(-193.94, 135.23) * mm, "end": v(-193.94, 133.19) * mm});
            skLineSegment(sketch, "E350", {"start": v(-193.94, 133.19) * mm, "end": v(-195.49, 133.19) * mm});
            skLineSegment(sketch, "E351", {"start": v(-195.49, 133.19) * mm, "end": v(-195.46, 131.47) * mm});
            skPoint(sketch, "E352.oppositeSnap0", {"position": v(-183.64, 140.68) * mm});
            skLineSegment(sketch, "E352.bottom", {"start": v(-187.7, 142.6) * mm, "end": v(-189.2, 142.6) * mm});
            skLineSegment(sketch, "E352.top", {"start": v(-187.7, 140.68) * mm, "end": v(-189.2, 140.68) * mm});
            skLineSegment(sketch, "E352.left", {"start": v(-187.7, 142.6) * mm, "end": v(-187.7, 140.68) * mm});
            skLineSegment(sketch, "E352.right", {"start": v(-189.2, 142.6) * mm, "end": v(-189.2, 140.68) * mm});
            skLineSegment(sketch, "E353.bottom", {"start": v(-189.2, 140.74) * mm, "end": v(-197.21, 140.74) * mm});
            skLineSegment(sketch, "E353.top", {"start": v(-189.2, 138.78) * mm, "end": v(-197.21, 138.78) * mm});
            skLineSegment(sketch, "E353.left", {"start": v(-189.2, 140.74) * mm, "end": v(-189.2, 138.78) * mm});
            skLineSegment(sketch, "E353.right", {"start": v(-197.21, 140.74) * mm, "end": v(-197.21, 138.78) * mm});
            skLineSegment(sketch, "E354.bottom", {"start": v(-195.49, 138.78) * mm, "end": v(-193.94, 138.78) * mm});
            skLineSegment(sketch, "E354.right", {"start": v(-193.94, 138.78) * mm, "end": v(-193.94, 135.23) * mm});
            skLineSegment(sketch, "E355.bottom", {"start": v(-193.94, 135.23) * mm, "end": v(-192.36, 135.23) * mm});
            skLineSegment(sketch, "E355.top", {"start": v(-193.94, 133.2) * mm, "end": v(-192.36, 133.2) * mm});
            skLineSegment(sketch, "E355.left", {"start": v(-193.94, 135.23) * mm, "end": v(-193.94, 133.2) * mm});
            skLineSegment(sketch, "E355.right", {"start": v(-192.36, 135.23) * mm, "end": v(-192.36, 133.2) * mm});
            skLineSegment(sketch, "E356.bottom", {"start": v(-192.36, 135.23) * mm, "end": v(-190.71, 135.23) * mm});
            skLineSegment(sketch, "E356.top", {"start": v(-192.36, 137) * mm, "end": v(-190.71, 137) * mm});
            skLineSegment(sketch, "E356.left", {"start": v(-192.36, 135.23) * mm, "end": v(-192.36, 137) * mm});
            skLineSegment(sketch, "E356.right", {"start": v(-190.71, 135.23) * mm, "end": v(-190.71, 137) * mm});
            skLineSegment(sketch, "E357.bottom", {"start": v(-190.71, 135.23) * mm, "end": v(-189.23, 135.23) * mm});
            skLineSegment(sketch, "E357.top", {"start": v(-190.71, 131.47) * mm, "end": v(-189.23, 131.47) * mm});
            skLineSegment(sketch, "E357.left", {"start": v(-190.71, 135.23) * mm, "end": v(-190.71, 131.47) * mm});
            skLineSegment(sketch, "E357.right", {"start": v(-189.23, 135.23) * mm, "end": v(-189.23, 131.47) * mm});
            skLineSegment(sketch, "E358.bottom", {"start": v(-193.94, 131.47) * mm, "end": v(-190.71, 131.47) * mm});
            skLineSegment(sketch, "E358.top", {"start": v(-193.94, 133.2) * mm, "end": v(-190.71, 133.2) * mm});
            skLineSegment(sketch, "E358.left", {"start": v(-193.94, 131.47) * mm, "end": v(-193.94, 133.2) * mm});
            skLineSegment(sketch, "E358.right", {"start": v(-190.71, 131.47) * mm, "end": v(-190.71, 133.2) * mm});
            skLineSegment(sketch, "E359.bottom", {"start": v(-189.23, 133.2) * mm, "end": v(-187.65, 133.2) * mm});
            skLineSegment(sketch, "E359.top", {"start": v(-189.23, 131.47) * mm, "end": v(-187.65, 131.47) * mm});
            skLineSegment(sketch, "E359.left", {"start": v(-189.23, 133.2) * mm, "end": v(-189.23, 131.47) * mm});
            skLineSegment(sketch, "E359.right", {"start": v(-187.65, 133.2) * mm, "end": v(-187.65, 131.47) * mm});
            skLineSegment(sketch, "E360.bottom", {"start": v(-187.65, 133.2) * mm, "end": v(-189.23, 133.2) * mm});
            skLineSegment(sketch, "E360.top", {"start": v(-187.65, 135.23) * mm, "end": v(-189.23, 135.23) * mm});
            skLineSegment(sketch, "E360.left", {"start": v(-187.65, 133.2) * mm, "end": v(-187.65, 135.23) * mm});
            skLineSegment(sketch, "E360.right", {"start": v(-189.23, 133.2) * mm, "end": v(-189.23, 135.23) * mm});
            skLineSegment(sketch, "E361.bottom", {"start": v(-189.23, 135.23) * mm, "end": v(-187.65, 135.23) * mm});
            skLineSegment(sketch, "E361.top", {"start": v(-189.23, 136.97) * mm, "end": v(-187.65, 136.97) * mm});
            skLineSegment(sketch, "E361.left", {"start": v(-189.23, 135.23) * mm, "end": v(-189.23, 136.97) * mm});
            skLineSegment(sketch, "E361.right", {"start": v(-187.65, 135.23) * mm, "end": v(-187.65, 136.97) * mm});
            skLineSegment(sketch, "E362.bottom", {"start": v(-187.65, 135.23) * mm, "end": v(-186.05, 135.23) * mm});
            skLineSegment(sketch, "E362.top", {"start": v(-187.65, 131.47) * mm, "end": v(-186.05, 131.47) * mm});
            skLineSegment(sketch, "E362.left", {"start": v(-187.65, 135.23) * mm, "end": v(-187.65, 131.47) * mm});
            skLineSegment(sketch, "E362.right", {"start": v(-186.05, 135.23) * mm, "end": v(-186.05, 131.47) * mm});
            skLineSegment(sketch, "E363.bottom", {"start": v(-182.97, 131.47) * mm, "end": v(-184.48, 131.47) * mm});
            skLineSegment(sketch, "E363.top", {"start": v(-182.97, 135.23) * mm, "end": v(-184.48, 135.23) * mm});
            skLineSegment(sketch, "E363.left", {"start": v(-182.97, 131.47) * mm, "end": v(-182.97, 135.23) * mm});
            skLineSegment(sketch, "E363.right", {"start": v(-184.48, 131.47) * mm, "end": v(-184.48, 135.23) * mm});
            skLineSegment(sketch, "E364.bottom", {"start": v(-184.48, 133.35) * mm, "end": v(-186.05, 133.35) * mm});
            skLineSegment(sketch, "E364.top", {"start": v(-184.48, 131.47) * mm, "end": v(-186.05, 131.47) * mm});
            skLineSegment(sketch, "E364.left", {"start": v(-184.48, 133.35) * mm, "end": v(-184.48, 131.47) * mm});
            skLineSegment(sketch, "E364.right", {"start": v(-186.05, 133.35) * mm, "end": v(-186.05, 131.47) * mm});
            skLineSegment(sketch, "E365.bottom", {"start": v(-184.48, 135.23) * mm, "end": v(-182.97, 135.23) * mm});
            skLineSegment(sketch, "E365.top", {"start": v(-184.48, 137.02) * mm, "end": v(-182.97, 137.02) * mm});
            skLineSegment(sketch, "E365.left", {"start": v(-184.48, 135.23) * mm, "end": v(-184.48, 137.02) * mm});
            skLineSegment(sketch, "E365.right", {"start": v(-182.97, 135.23) * mm, "end": v(-182.97, 137.02) * mm});
            skLineSegment(sketch, "E366.bottom", {"start": v(-182.97, 131.47) * mm, "end": v(-181.32, 131.47) * mm});
            skLineSegment(sketch, "E366.top", {"start": v(-182.97, 135.23) * mm, "end": v(-181.32, 135.23) * mm});
            skLineSegment(sketch, "E366.right", {"start": v(-181.32, 131.47) * mm, "end": v(-181.32, 135.23) * mm});
            skLineSegment(sketch, "E367.bottom", {"start": v(-181.32, 135.23) * mm, "end": v(-179.76, 135.23) * mm});
            skLineSegment(sketch, "E367.top", {"start": v(-181.32, 137) * mm, "end": v(-179.76, 137) * mm});
            skLineSegment(sketch, "E367.left", {"start": v(-181.32, 135.23) * mm, "end": v(-181.32, 137) * mm});
            skLineSegment(sketch, "E367.right", {"start": v(-179.76, 135.23) * mm, "end": v(-179.76, 137) * mm});
            skLineSegment(sketch, "E368.bottom", {"start": v(-179.76, 135.23) * mm, "end": v(-178.1, 135.23) * mm});
            skLineSegment(sketch, "E368.top", {"start": v(-179.76, 133.2) * mm, "end": v(-178.1, 133.2) * mm});
            skLineSegment(sketch, "E368.left", {"start": v(-179.76, 135.23) * mm, "end": v(-179.76, 133.2) * mm});
            skLineSegment(sketch, "E368.right", {"start": v(-178.1, 135.23) * mm, "end": v(-178.1, 133.2) * mm});
            skLineSegment(sketch, "E369.bottom", {"start": v(-179.76, 133.2) * mm, "end": v(-181.32, 133.2) * mm});
            skLineSegment(sketch, "E369.top", {"start": v(-179.76, 135.23) * mm, "end": v(-181.32, 135.23) * mm});
            skLineSegment(sketch, "E369.left", {"start": v(-179.76, 133.2) * mm, "end": v(-179.76, 135.23) * mm});
            skLineSegment(sketch, "E369.right", {"start": v(-181.32, 133.2) * mm, "end": v(-181.32, 135.23) * mm});
            skLineSegment(sketch, "E370.bottom", {"start": v(-175.03, 140.68) * mm, "end": v(-182.97, 140.68) * mm});
            skLineSegment(sketch, "E370.top", {"start": v(-175.03, 138.78) * mm, "end": v(-182.97, 138.78) * mm});
            skLineSegment(sketch, "E370.left", {"start": v(-175.03, 140.68) * mm, "end": v(-175.03, 138.78) * mm});
            skLineSegment(sketch, "E370.right", {"start": v(-182.97, 140.68) * mm, "end": v(-182.97, 138.78) * mm});
            skLineSegment(sketch, "E371.bottom", {"start": v(-176.54, 138.78) * mm, "end": v(-178.1, 138.78) * mm});
            skLineSegment(sketch, "E371.top", {"start": v(-176.54, 135.23) * mm, "end": v(-178.1, 135.23) * mm});
            skLineSegment(sketch, "E371.left", {"start": v(-176.54, 138.78) * mm, "end": v(-176.54, 135.23) * mm});
            skLineSegment(sketch, "E371.right", {"start": v(-178.1, 138.78) * mm, "end": v(-178.1, 135.23) * mm});
            skLineSegment(sketch, "E372.bottom", {"start": v(-178.1, 133.2) * mm, "end": v(-176.72, 133.2) * mm});
            skLineSegment(sketch, "E372.top", {"start": v(-178.1, 131.47) * mm, "end": v(-176.72, 131.47) * mm});
            skLineSegment(sketch, "E372.left", {"start": v(-178.1, 133.2) * mm, "end": v(-178.1, 131.47) * mm});
            skLineSegment(sketch, "E372.right", {"start": v(-176.72, 133.2) * mm, "end": v(-176.72, 131.47) * mm});
            skLineSegment(sketch, "E373.bottom", {"start": v(-198.71, 151.83) * mm, "end": v(-200.26, 151.83) * mm});
            skLineSegment(sketch, "E373.top", {"start": v(-198.71, 149.83) * mm, "end": v(-203.5, 149.83) * mm});
            skLineSegment(sketch, "E373.left", {"start": v(-198.71, 151.83) * mm, "end": v(-198.71, 149.83) * mm});
            skLineSegment(sketch, "E373.right", {"start": v(-203.5, 151.83) * mm, "end": v(-203.5, 149.83) * mm});
            skLineSegment(sketch, "E374.bottom", {"start": v(-200.26, 153.62) * mm, "end": v(-203.5, 153.62) * mm});
            skLineSegment(sketch, "E374.top", {"start": v(-203.5, 151.83) * mm, "end": v(-204.99, 151.83) * mm});
            skLineSegment(sketch, "E374.left", {"start": v(-200.26, 153.62) * mm, "end": v(-200.26, 151.83) * mm});
            skLineSegment(sketch, "E374.right", {"start": v(-204.99, 153.62) * mm, "end": v(-204.99, 151.83) * mm});
            skLineSegment(sketch, "E375.bottom", {"start": v(-203.5, 155.43) * mm, "end": v(-206.66, 155.43) * mm});
            skLineSegment(sketch, "E375.top", {"start": v(-204.99, 153.62) * mm, "end": v(-206.66, 153.62) * mm});
            skLineSegment(sketch, "E375.left", {"start": v(-203.5, 155.43) * mm, "end": v(-203.5, 153.62) * mm});
            skLineSegment(sketch, "E375.right", {"start": v(-206.66, 155.43) * mm, "end": v(-206.66, 153.62) * mm});
            skLineSegment(sketch, "E376.bottom", {"start": v(-206.66, 155.43) * mm, "end": v(-208.24, 155.43) * mm});
            skLineSegment(sketch, "E376.top", {"start": v(-206.66, 157.23) * mm, "end": v(-208.24, 157.23) * mm});
            skLineSegment(sketch, "E376.left", {"start": v(-206.66, 155.43) * mm, "end": v(-206.66, 157.23) * mm});
            skLineSegment(sketch, "E376.right", {"start": v(-208.24, 155.43) * mm, "end": v(-208.24, 157.23) * mm});
            skLineSegment(sketch, "E377", {"start": v(-187.7, 148.06) * mm, "end": v(-189.18, 148.06) * mm});
            skLineSegment(sketch, "E378", {"start": v(-189.18, 148.06) * mm, "end": v(-189.18, 149.9) * mm});
            skLineSegment(sketch, "E379", {"start": v(-178.1, 144.37) * mm, "end": v(-178.1, 142.54) * mm});
            skLineSegment(sketch, "E380", {"start": v(-178.1, 142.54) * mm, "end": v(-179.71, 142.54) * mm});
            skLineSegment(sketch, "E381", {"start": v(-179.71, 142.54) * mm, "end": v(-179.71, 144.35) * mm});
            skLineSegment(sketch, "E382", {"start": v(-179.71, 144.35) * mm, "end": v(-178.1, 144.37) * mm});
            skPoint(sketch, "E383.oppositeSnap0", {"position": v(-157.55, 125.14) * mm});
            skLineSegment(sketch, "E383.bottom", {"start": v(-155.93, 122.28) * mm, "end": v(-157.55, 122.28) * mm});
            skLineSegment(sketch, "E383.top", {"start": v(-155.93, 120.5) * mm, "end": v(-157.55, 120.5) * mm});
            skLineSegment(sketch, "E383.left", {"start": v(-155.93, 122.28) * mm, "end": v(-155.93, 120.5) * mm});
            skLineSegment(sketch, "E383.right", {"start": v(-157.55, 122.28) * mm, "end": v(-157.55, 120.5) * mm});
            skLineSegment(sketch, "E384.bottom", {"start": v(-157.55, 122.28) * mm, "end": v(-159.1, 122.28) * mm});
            skLineSegment(sketch, "E384.top", {"start": v(-157.55, 123.98) * mm, "end": v(-159.1, 123.98) * mm});
            skLineSegment(sketch, "E384.left", {"start": v(-157.55, 122.28) * mm, "end": v(-157.55, 123.98) * mm});
            skLineSegment(sketch, "E384.right", {"start": v(-159.1, 122.28) * mm, "end": v(-159.1, 123.98) * mm});
            skLineSegment(sketch, "E385.bottom", {"start": v(-159.1, 123.98) * mm, "end": v(-160.69, 123.98) * mm});
            skLineSegment(sketch, "E385.top", {"start": v(-159.1, 126) * mm, "end": v(-160.69, 126) * mm});
            skLineSegment(sketch, "E385.left", {"start": v(-159.1, 123.98) * mm, "end": v(-159.1, 126) * mm});
            skLineSegment(sketch, "E385.right", {"start": v(-160.69, 123.98) * mm, "end": v(-160.69, 126) * mm});
            skLineSegment(sketch, "E386.bottom", {"start": v(-162.31, 123.98) * mm, "end": v(-164, 123.98) * mm});
            skLineSegment(sketch, "E386.top", {"start": v(-162.31, 122.28) * mm, "end": v(-164, 122.28) * mm});
            skLineSegment(sketch, "E386.left", {"start": v(-162.31, 123.98) * mm, "end": v(-162.31, 122.28) * mm});
            skLineSegment(sketch, "E386.right", {"start": v(-164, 123.98) * mm, "end": v(-164, 122.28) * mm});
            skLineSegment(sketch, "E387.bottom", {"start": v(-164, 126) * mm, "end": v(-168.7, 126) * mm});
            skLineSegment(sketch, "E387.top", {"start": v(-164, 123.98) * mm, "end": v(-168.7, 123.98) * mm});
            skLineSegment(sketch, "E387.left", {"start": v(-164, 126) * mm, "end": v(-164, 123.98) * mm});
            skLineSegment(sketch, "E387.right", {"start": v(-168.7, 126) * mm, "end": v(-168.7, 123.98) * mm});
            skLineSegment(sketch, "E388.bottom", {"start": v(-171.87, 126) * mm, "end": v(-173.4, 126) * mm});
            skLineSegment(sketch, "E388.top", {"start": v(-171.87, 123.98) * mm, "end": v(-173.4, 123.98) * mm});
            skLineSegment(sketch, "E388.left", {"start": v(-171.87, 126) * mm, "end": v(-171.87, 123.98) * mm});
            skLineSegment(sketch, "E388.right", {"start": v(-173.4, 126) * mm, "end": v(-173.4, 123.98) * mm});
            skLineSegment(sketch, "E389.bottom", {"start": v(-171.87, 123.98) * mm, "end": v(-170.19, 123.98) * mm});
            skLineSegment(sketch, "E389.top", {"start": v(-171.87, 122.28) * mm, "end": v(-170.19, 122.28) * mm});
            skLineSegment(sketch, "E389.left", {"start": v(-171.87, 123.98) * mm, "end": v(-171.87, 122.28) * mm});
            skLineSegment(sketch, "E389.right", {"start": v(-170.19, 123.98) * mm, "end": v(-170.19, 122.28) * mm});
            skLineSegment(sketch, "E390", {"start": v(-160.69, 129.58) * mm, "end": v(-160.85, 135.26) * mm});
            skLineSegment(sketch, "E391", {"start": v(-160.85, 135.26) * mm, "end": v(-162.35, 135.21) * mm});
            skLineSegment(sketch, "E392", {"start": v(-162.35, 135.21) * mm, "end": v(-162.42, 137.1) * mm});
            skLineSegment(sketch, "E393", {"start": v(-162.42, 137.1) * mm, "end": v(-163.91, 137.04) * mm});
            skLineSegment(sketch, "E394", {"start": v(-163.91, 137.04) * mm, "end": v(-163.93, 138.9) * mm});
            skLineSegment(sketch, "E395", {"start": v(-165.4, 138.9) * mm, "end": v(-163.92, 138.9) * mm});
            skLineSegment(sketch, "E396", {"start": v(-165.4, 138.9) * mm, "end": v(-165.45, 140.88) * mm});
            skLineSegment(sketch, "E397.bottom", {"start": v(-165.45, 142.6) * mm, "end": v(-167.05, 142.6) * mm});
            skLineSegment(sketch, "E397.top", {"start": v(-165.45, 140.73) * mm, "end": v(-167.05, 140.73) * mm});
            skLineSegment(sketch, "E397.left", {"start": v(-165.45, 142.6) * mm, "end": v(-165.45, 140.73) * mm});
            skLineSegment(sketch, "E397.right", {"start": v(-167.05, 142.6) * mm, "end": v(-167.05, 140.73) * mm});
            skLineSegment(sketch, "E398.bottom", {"start": v(-198.83, 137.07) * mm, "end": v(-200.23, 137.07) * mm});
            skLineSegment(sketch, "E398.top", {"start": v(-198.83, 135.07) * mm, "end": v(-200.23, 135.07) * mm});
            skLineSegment(sketch, "E398.left", {"start": v(-198.83, 137.07) * mm, "end": v(-198.83, 135.07) * mm});
            skLineSegment(sketch, "E398.right", {"start": v(-200.23, 137.07) * mm, "end": v(-200.23, 135.07) * mm});
            skLineSegment(sketch, "E399.bottom", {"start": v(-203.5, 142.58) * mm, "end": v(-209.92, 142.58) * mm});
            skLineSegment(sketch, "E399.top", {"start": v(-203.5, 140.82) * mm, "end": v(-209.92, 140.82) * mm});
            skLineSegment(sketch, "E399.left", {"start": v(-203.5, 142.58) * mm, "end": v(-203.5, 140.82) * mm});
            skLineSegment(sketch, "E399.right", {"start": v(-209.92, 142.58) * mm, "end": v(-209.92, 140.82) * mm});
            skLineSegment(sketch, "E400.top", {"start": v(-209.92, 138.95) * mm, "end": v(-212.98, 138.95) * mm});
            skLineSegment(sketch, "E400.left", {"start": v(-209.92, 140.82) * mm, "end": v(-209.92, 138.95) * mm});
            skLineSegment(sketch, "E401.top", {"start": v(-212.98, 135.24) * mm, "end": v(-214.55, 135.24) * mm});
            skLineSegment(sketch, "E401.left", {"start": v(-212.98, 138.95) * mm, "end": v(-212.98, 135.24) * mm});
            skLineSegment(sketch, "E401.right", {"start": v(-214.55, 138.95) * mm, "end": v(-214.55, 135.24) * mm});
            skLineSegment(sketch, "E402.bottom", {"start": v(-154.5, 162.92) * mm, "end": v(-155.95, 162.92) * mm});
            skLineSegment(sketch, "E402.top", {"start": v(-154.5, 161) * mm, "end": v(-155.95, 161) * mm});
            skLineSegment(sketch, "E402.left", {"start": v(-154.5, 162.92) * mm, "end": v(-154.5, 161) * mm});
            skLineSegment(sketch, "E402.right", {"start": v(-155.95, 162.92) * mm, "end": v(-155.95, 161) * mm});
            skLineSegment(sketch, "E403.bottom", {"start": v(-155.86, 168.47) * mm, "end": v(-159.32, 168.47) * mm});
            skLineSegment(sketch, "E403.top", {"start": v(-157.56, 164.37) * mm, "end": v(-159.32, 164.37) * mm});
            skLineSegment(sketch, "E403.left", {"start": v(-155.86, 168.47) * mm, "end": v(-155.86, 164.37) * mm});
            skLineSegment(sketch, "E403.right", {"start": v(-159.32, 168.47) * mm, "end": v(-159.32, 164.37) * mm});
            skLineSegment(sketch, "E404.top", {"start": v(-155.86, 162.82) * mm, "end": v(-157.56, 162.82) * mm});
            skLineSegment(sketch, "E404.left", {"start": v(-155.86, 164.37) * mm, "end": v(-155.86, 162.82) * mm});
            skLineSegment(sketch, "E404.right", {"start": v(-157.56, 164.37) * mm, "end": v(-157.56, 162.82) * mm});
            skLineSegment(sketch, "E405", {"start": v(-203.43, 166.58) * mm, "end": v(-203.43, 164.67) * mm});
            skLineSegment(sketch, "E406", {"start": v(-203.43, 164.67) * mm, "end": v(-204.98, 164.65) * mm});
            skLineSegment(sketch, "E407.bottom", {"start": v(-208.22, 164.65) * mm, "end": v(-204.96, 164.65) * mm});
            skLineSegment(sketch, "E407.top", {"start": v(-208.22, 162.72) * mm, "end": v(-204.96, 162.72) * mm});
            skLineSegment(sketch, "E407.left", {"start": v(-208.22, 164.65) * mm, "end": v(-208.22, 162.72) * mm});
            skLineSegment(sketch, "E407.right", {"start": v(-204.96, 164.65) * mm, "end": v(-204.96, 162.72) * mm});
            skLineSegment(sketch, "E408.bottom", {"start": v(-209.87, 162.8) * mm, "end": v(-208.22, 162.8) * mm});
            skLineSegment(sketch, "E408.top", {"start": v(-209.87, 161.02) * mm, "end": v(-208.22, 161.02) * mm});
            skLineSegment(sketch, "E408.left", {"start": v(-209.87, 162.8) * mm, "end": v(-209.87, 161.02) * mm});
            skLineSegment(sketch, "E408.right", {"start": v(-208.22, 162.8) * mm, "end": v(-208.22, 161.02) * mm});
            skLineSegment(sketch, "E409.bottom", {"start": v(-213.02, 161.04) * mm, "end": v(-209.87, 161.04) * mm});
            skLineSegment(sketch, "E409.top", {"start": v(-213.02, 159.13) * mm, "end": v(-209.87, 159.13) * mm});
            skLineSegment(sketch, "E409.left", {"start": v(-213.02, 161.04) * mm, "end": v(-213.02, 159.13) * mm});
            skLineSegment(sketch, "E409.right", {"start": v(-209.87, 161.04) * mm, "end": v(-209.87, 159.13) * mm});
            skLineSegment(sketch, "E410.bottom", {"start": v(-214.62, 159.15) * mm, "end": v(-213.02, 159.15) * mm});
            skLineSegment(sketch, "E410.top", {"start": v(-214.62, 157.26) * mm, "end": v(-213.02, 157.26) * mm});
            skLineSegment(sketch, "E410.left", {"start": v(-214.62, 159.15) * mm, "end": v(-214.62, 157.26) * mm});
            skLineSegment(sketch, "E410.right", {"start": v(-213.02, 159.15) * mm, "end": v(-213.02, 157.26) * mm});
            skLineSegment(sketch, "E411.bottom", {"start": v(-152.88, 172.1) * mm, "end": v(-154.5, 172.1) * mm});
            skLineSegment(sketch, "E411.top", {"start": v(-152.88, 168.3) * mm, "end": v(-154.5, 168.3) * mm});
            skLineSegment(sketch, "E411.left", {"start": v(-152.88, 172.1) * mm, "end": v(-152.88, 168.3) * mm});
            skLineSegment(sketch, "E411.right", {"start": v(-154.5, 172.1) * mm, "end": v(-154.5, 168.3) * mm});
            skLineSegment(sketch, "E412.bottom", {"start": v(-154.5, 170.2) * mm, "end": v(-155.86, 170.2) * mm});
            skLineSegment(sketch, "E412.top", {"start": v(-154.5, 168.25) * mm, "end": v(-155.86, 168.25) * mm});
            skLineSegment(sketch, "E412.left", {"start": v(-154.5, 170.2) * mm, "end": v(-154.5, 168.25) * mm});
            skLineSegment(sketch, "E412.right", {"start": v(-155.86, 170.2) * mm, "end": v(-155.86, 168.25) * mm});
            skLineSegment(sketch, "E413.bottom", {"start": v(-155.86, 175.8) * mm, "end": v(-157.61, 175.8) * mm});
            skLineSegment(sketch, "E413.top", {"start": v(-155.86, 173.9) * mm, "end": v(-157.61, 173.9) * mm});
            skLineSegment(sketch, "E413.left", {"start": v(-155.86, 175.8) * mm, "end": v(-155.86, 173.9) * mm});
            skLineSegment(sketch, "E413.right", {"start": v(-157.61, 175.8) * mm, "end": v(-157.61, 173.9) * mm});
            skLineSegment(sketch, "E414.bottom", {"start": v(-157.61, 173.9) * mm, "end": v(-159.15, 173.9) * mm});
            skLineSegment(sketch, "E414.top", {"start": v(-157.61, 172.04) * mm, "end": v(-159.15, 172.04) * mm});
            skLineSegment(sketch, "E414.left", {"start": v(-157.61, 173.9) * mm, "end": v(-157.61, 172.04) * mm});
            skLineSegment(sketch, "E414.right", {"start": v(-159.15, 173.9) * mm, "end": v(-159.15, 172.04) * mm});
            skLineSegment(sketch, "E415.bottom", {"start": v(-159.15, 172.04) * mm, "end": v(-160.7, 172.04) * mm});
            skLineSegment(sketch, "E415.top", {"start": v(-159.15, 170.12) * mm, "end": v(-160.7, 170.12) * mm});
            skLineSegment(sketch, "E415.left", {"start": v(-159.15, 172.04) * mm, "end": v(-159.15, 170.12) * mm});
            skLineSegment(sketch, "E415.right", {"start": v(-160.7, 172.04) * mm, "end": v(-160.7, 170.12) * mm});
            skLineSegment(sketch, "E416.bottom", {"start": v(-160.7, 172.04) * mm, "end": v(-165.6, 172.04) * mm});
            skLineSegment(sketch, "E416.top", {"start": v(-160.7, 173.8) * mm, "end": v(-165.6, 173.8) * mm});
            skLineSegment(sketch, "E416.left", {"start": v(-160.7, 172.04) * mm, "end": v(-160.7, 173.8) * mm});
            skLineSegment(sketch, "E416.right", {"start": v(-165.6, 172.04) * mm, "end": v(-165.6, 173.8) * mm});
            skLineSegment(sketch, "E417.bottom", {"start": v(-162.32, 173.8) * mm, "end": v(-164, 173.8) * mm});
            skLineSegment(sketch, "E417.top", {"start": v(-162.32, 175.72) * mm, "end": v(-164, 175.72) * mm});
            skLineSegment(sketch, "E417.left", {"start": v(-162.32, 173.8) * mm, "end": v(-162.32, 175.72) * mm});
            skLineSegment(sketch, "E417.right", {"start": v(-164, 173.8) * mm, "end": v(-164, 175.72) * mm});
            skLineSegment(sketch, "E418.bottom", {"start": v(-162.32, 175.72) * mm, "end": v(-160.7, 175.72) * mm});
            skLineSegment(sketch, "E418.top", {"start": v(-162.32, 177.5) * mm, "end": v(-160.7, 177.5) * mm});
            skLineSegment(sketch, "E418.left", {"start": v(-162.32, 175.72) * mm, "end": v(-162.32, 177.5) * mm});
            skLineSegment(sketch, "E418.right", {"start": v(-160.7, 175.72) * mm, "end": v(-160.7, 177.5) * mm});
            skLineSegment(sketch, "E419", {"start": v(-170.05, 168.34) * mm, "end": v(-170.05, 166.57) * mm});
            skLineSegment(sketch, "E420", {"start": v(-170.05, 166.57) * mm, "end": v(-173.36, 166.57) * mm});
            skLineSegment(sketch, "E421", {"start": v(-173.36, 166.57) * mm, "end": v(-173.36, 164.64) * mm});
            skLineSegment(sketch, "E422", {"start": v(-173.36, 164.64) * mm, "end": v(-171.7, 164.64) * mm});
            skLineSegment(sketch, "E423", {"start": v(-171.7, 164.64) * mm, "end": v(-171.7, 159.07) * mm});
            skLineSegment(sketch, "E424", {"start": v(-171.7, 159.07) * mm, "end": v(-173.5, 159.07) * mm});
            skLineSegment(sketch, "E425", {"start": v(-173.5, 159.07) * mm, "end": v(-173.5, 157.18) * mm});
            skLineSegment(sketch, "E426", {"start": v(-173.5, 157.18) * mm, "end": v(-175.04, 157.18) * mm});
            skLineSegment(sketch, "E427", {"start": v(-175.04, 157.18) * mm, "end": v(-175.04, 155.5) * mm});
            skLineSegment(sketch, "E428", {"start": v(-175.04, 155.5) * mm, "end": v(-178.19, 155.5) * mm});
            skLineSegment(sketch, "E429", {"start": v(-178.19, 155.5) * mm, "end": v(-178.19, 153.8) * mm});
            skLineSegment(sketch, "E430", {"start": v(-178.19, 153.8) * mm, "end": v(-192.34, 153.8) * mm});
            skLineSegment(sketch, "E431", {"start": v(-192.34, 153.8) * mm, "end": v(-192.34, 155.34) * mm});
            skLineSegment(sketch, "E432", {"start": v(-192.34, 155.34) * mm, "end": v(-197.29, 155.34) * mm});
            skLineSegment(sketch, "E433", {"start": v(-197.29, 155.34) * mm, "end": v(-197.29, 157.24) * mm});
            skLineSegment(sketch, "E434", {"start": v(-197.29, 157.24) * mm, "end": v(-198.83, 157.24) * mm});
            skLineSegment(sketch, "E435", {"start": v(-198.83, 157.24) * mm, "end": v(-198.83, 159.2) * mm});
            skLineSegment(sketch, "E436", {"start": v(-198.83, 159.2) * mm, "end": v(-200.44, 159.2) * mm});
            skLineSegment(sketch, "E437", {"start": v(-200.44, 159.2) * mm, "end": v(-200.44, 164.67) * mm});
            skLineSegment(sketch, "E438", {"start": v(-200.44, 164.67) * mm, "end": v(-198.8, 164.67) * mm});
            skLineSegment(sketch, "E439", {"start": v(-198.8, 164.67) * mm, "end": v(-198.8, 166.4) * mm});
            skLineSegment(sketch, "E440", {"start": v(-198.8, 166.4) * mm, "end": v(-201.87, 166.4) * mm});
            skLineSegment(sketch, "E441", {"start": v(-201.87, 166.4) * mm, "end": v(-201.87, 166.58) * mm});
            skLineSegment(sketch, "E442", {"start": v(-182.92, 149.87) * mm, "end": v(-182.92, 148.06) * mm});
            skLineSegment(sketch, "E443", {"start": v(-181.27, 149.87) * mm, "end": v(-181.27, 148.06) * mm});
            skLineSegment(sketch, "E444", {"start": v(-176.62, 149.87) * mm, "end": v(-176.62, 148.06) * mm});
            skLineSegment(sketch, "E445", {"start": v(-175.03, 148.06) * mm, "end": v(-176.62, 148.06) * mm});
            skLineSegment(sketch, "E446", {"start": v(-178.14, 149.87) * mm, "end": v(-178.14, 148.06) * mm});
            skLineSegment(sketch, "E447", {"start": v(-179.76, 149.87) * mm, "end": v(-179.76, 148.06) * mm});
            skLineSegment(sketch, "E448", {"start": v(-216.22, 129.7) * mm, "end": v(-214.51, 129.7) * mm});
            skLineSegment(sketch, "E449", {"start": v(-214.51, 129.7) * mm, "end": v(-214.51, 127.77) * mm});
            skLineSegment(sketch, "E450", {"start": v(-214.51, 127.77) * mm, "end": v(-216.22, 127.77) * mm});
            skLineSegment(sketch, "E451", {"start": v(-216.22, 127.77) * mm, "end": v(-216.22, 126.05) * mm});
            skLineSegment(sketch, "E452", {"start": v(-216.22, 126.05) * mm, "end": v(-214.67, 126.05) * mm});
            skLineSegment(sketch, "E453", {"start": v(-214.67, 126.05) * mm, "end": v(-214.67, 127.77) * mm});
            skLineSegment(sketch, "E454", {"start": v(-214.67, 127.77) * mm, "end": v(-214.51, 127.77) * mm});
            skLineSegment(sketch, "E455.bottom", {"start": v(-211.56, 124.17) * mm, "end": v(-209.87, 124.17) * mm});
            skLineSegment(sketch, "E455.top", {"start": v(-211.56, 125.98) * mm, "end": v(-209.87, 125.98) * mm});
            skLineSegment(sketch, "E455.left", {"start": v(-211.56, 124.17) * mm, "end": v(-211.56, 125.98) * mm});
            skLineSegment(sketch, "E455.right", {"start": v(-209.87, 124.17) * mm, "end": v(-209.87, 125.98) * mm});
            skLineSegment(sketch, "E456.bottom", {"start": v(-189.29, 172.08) * mm, "end": v(-186.1, 172.08) * mm});
            skLineSegment(sketch, "E456.top", {"start": v(-189.29, 168.3) * mm, "end": v(-186.1, 168.3) * mm});
            skLineSegment(sketch, "E456.left", {"start": v(-189.29, 172.08) * mm, "end": v(-189.29, 168.3) * mm});
            skLineSegment(sketch, "E456.right", {"start": v(-186.1, 172.08) * mm, "end": v(-186.1, 168.3) * mm});
            skLineSegment(sketch, "E457.bottom", {"start": v(-184.58, 172.13) * mm, "end": v(-181.34, 172.13) * mm});
            skLineSegment(sketch, "E457.top", {"start": v(-184.58, 168.35) * mm, "end": v(-181.34, 168.35) * mm});
            skLineSegment(sketch, "E457.left", {"start": v(-184.58, 172.13) * mm, "end": v(-184.58, 168.35) * mm});
            skLineSegment(sketch, "E457.right", {"start": v(-181.34, 172.13) * mm, "end": v(-181.34, 168.35) * mm});
            skLineSegment(sketch, "E458.bottom", {"start": v(-186.1, 168.3) * mm, "end": v(-187.66, 168.3) * mm});
            skLineSegment(sketch, "E458.top", {"start": v(-186.1, 170.19) * mm, "end": v(-187.66, 170.19) * mm});
            skLineSegment(sketch, "E458.left", {"start": v(-186.1, 168.3) * mm, "end": v(-186.1, 170.19) * mm});
            skLineSegment(sketch, "E458.right", {"start": v(-187.66, 168.3) * mm, "end": v(-187.66, 170.19) * mm});
            skLineSegment(sketch, "E459.bottom", {"start": v(-184.58, 168.35) * mm, "end": v(-182.82, 168.35) * mm});
            skLineSegment(sketch, "E459.top", {"start": v(-184.58, 170.24) * mm, "end": v(-182.82, 170.24) * mm});
            skLineSegment(sketch, "E459.left", {"start": v(-184.58, 168.35) * mm, "end": v(-184.58, 170.24) * mm});
            skLineSegment(sketch, "E459.right", {"start": v(-182.82, 168.35) * mm, "end": v(-182.82, 170.24) * mm});
            skLineSegment(sketch, "E460.bottom", {"start": v(-192.42, 166.43) * mm, "end": v(-197.26, 166.43) * mm});
            skLineSegment(sketch, "E460.top", {"start": v(-192.42, 170.13) * mm, "end": v(-194, 170.13) * mm});
            skLineSegment(sketch, "E460.left", {"start": v(-192.42, 166.43) * mm, "end": v(-192.42, 170.13) * mm});
            skLineSegment(sketch, "E460.right", {"start": v(-197.26, 166.43) * mm, "end": v(-197.26, 170.13) * mm});
            skLineSegment(sketch, "E461.bottom", {"start": v(-197.26, 170.13) * mm, "end": v(-194, 170.13) * mm});
            skLineSegment(sketch, "E461.top", {"start": v(-197.26, 172.07) * mm, "end": v(-195.52, 172.07) * mm});
            skLineSegment(sketch, "E461.left", {"start": v(-197.26, 170.13) * mm, "end": v(-197.26, 172.07) * mm});
            skLineSegment(sketch, "E461.right", {"start": v(-194, 170.13) * mm, "end": v(-194, 172.07) * mm});
            skLineSegment(sketch, "E462.bottom", {"start": v(-195.52, 173.99) * mm, "end": v(-193.82, 173.99) * mm});
            skLineSegment(sketch, "E462.top", {"start": v(-195.52, 172.07) * mm, "end": v(-192.42, 172.07) * mm});
            skLineSegment(sketch, "E462.right", {"start": v(-192.42, 173.99) * mm, "end": v(-192.42, 172.07) * mm});
            skLineSegment(sketch, "E463.bottom", {"start": v(-193.82, 175.67) * mm, "end": v(-190.85, 175.67) * mm});
            skLineSegment(sketch, "E463.top", {"start": v(-193.82, 173.99) * mm, "end": v(-190.85, 173.99) * mm});
            skLineSegment(sketch, "E463.right", {"start": v(-190.85, 175.67) * mm, "end": v(-190.85, 173.99) * mm});
            skLineSegment(sketch, "E464.bottom", {"start": v(-192.33, 177.58) * mm, "end": v(-190.68, 177.58) * mm});
            skLineSegment(sketch, "E464.right", {"start": v(-178.08, 177.58) * mm, "end": v(-178.08, 175.67) * mm});
            skLineSegment(sketch, "E465.bottom", {"start": v(-186.1, 172.08) * mm, "end": v(-184.58, 172.08) * mm});
            skLineSegment(sketch, "E465.left", {"start": v(-186.1, 172.08) * mm, "end": v(-186.1, 173.99) * mm});
            skLineSegment(sketch, "E465.right", {"start": v(-184.58, 172.08) * mm, "end": v(-184.58, 173.99) * mm});
            skLineSegment(sketch, "E466.top", {"start": v(-184.58, 173.99) * mm, "end": v(-182.88, 173.99) * mm});
            skLineSegment(sketch, "E466.right", {"start": v(-182.88, 175.67) * mm, "end": v(-182.88, 173.99) * mm});
            skLineSegment(sketch, "E467.top", {"start": v(-186.1, 173.99) * mm, "end": v(-187.66, 173.99) * mm});
            skLineSegment(sketch, "E467.right", {"start": v(-187.66, 175.67) * mm, "end": v(-187.66, 173.99) * mm});
            skLineSegment(sketch, "E468.left", {"start": v(-179.8, 175.67) * mm, "end": v(-179.8, 173.81) * mm});
            skLineSegment(sketch, "E468.right", {"start": v(-176.61, 175.67) * mm, "end": v(-176.61, 173.81) * mm});
            skLineSegment(sketch, "E469.bottom", {"start": v(-174.95, 173.81) * mm, "end": v(-178.08, 173.81) * mm});
            skLineSegment(sketch, "E469.top", {"start": v(-176.61, 172.07) * mm, "end": v(-178.08, 172.07) * mm});
            skLineSegment(sketch, "E469.left", {"start": v(-174.95, 173.81) * mm, "end": v(-174.95, 172.07) * mm});
            skLineSegment(sketch, "E469.right", {"start": v(-178.08, 173.81) * mm, "end": v(-178.08, 172.07) * mm});
            skLineSegment(sketch, "E470.top", {"start": v(-174.95, 166.43) * mm, "end": v(-176.61, 166.43) * mm});
            skLineSegment(sketch, "E470.left", {"start": v(-174.95, 171.97) * mm, "end": v(-174.95, 166.43) * mm});
            skLineSegment(sketch, "E470.right", {"start": v(-176.61, 171.97) * mm, "end": v(-176.61, 170.2) * mm});
            skLineSegment(sketch, "E471.left", {"start": v(-176.61, 171.97) * mm, "end": v(-176.61, 172.07) * mm});
            skLineSegment(sketch, "E471.right", {"start": v(-174.95, 171.97) * mm, "end": v(-174.95, 172.07) * mm});
            skLineSegment(sketch, "E472.bottom", {"start": v(-176.61, 166.43) * mm, "end": v(-178.16, 166.43) * mm});
            skLineSegment(sketch, "E472.top", {"start": v(-176.61, 170.2) * mm, "end": v(-178.16, 170.2) * mm});
            skLineSegment(sketch, "E472.right", {"start": v(-178.16, 166.43) * mm, "end": v(-178.16, 170.2) * mm});
            skLineSegment(sketch, "E473.trimOffspring", {"start": v(-182.88, 175.67) * mm, "end": v(-179.8, 175.67) * mm});
            skPoint(sketch, "E474.orphan", {"position": v(-184.58, 175.67) * mm});
            skLineSegment(sketch, "E475.bottom", {"start": v(-187.7, 166.5) * mm, "end": v(-182.87, 166.5) * mm});
            skLineSegment(sketch, "E475.top", {"start": v(-187.7, 164.5) * mm, "end": v(-182.87, 164.5) * mm});
            skLineSegment(sketch, "E475.left", {"start": v(-187.7, 166.5) * mm, "end": v(-187.7, 164.5) * mm});
            skLineSegment(sketch, "E475.right", {"start": v(-182.87, 166.5) * mm, "end": v(-182.87, 164.5) * mm});
            skLineSegment(sketch, "E476.top", {"start": v(-195.57, 157.2) * mm, "end": v(-192.45, 157.2) * mm});
            skLineSegment(sketch, "E476.left", {"start": v(-195.57, 159.07) * mm, "end": v(-195.57, 157.2) * mm});
            skLineSegment(sketch, "E476.right", {"start": v(-192.45, 159.07) * mm, "end": v(-192.45, 157.2) * mm});
            skLineSegment(sketch, "E477.top", {"start": v(-190.81, 155.43) * mm, "end": v(-186.05, 155.43) * mm});
            skLineSegment(sketch, "E477.left", {"start": v(-190.81, 159.2) * mm, "end": v(-190.81, 155.43) * mm});
            skLineSegment(sketch, "E477.right", {"start": v(-186.05, 159.2) * mm, "end": v(-186.05, 155.43) * mm});
            skLineSegment(sketch, "E478.bottom", {"start": v(-184.45, 159.16) * mm, "end": v(-182.78, 159.16) * mm});
            skLineSegment(sketch, "E478.top", {"start": v(-184.45, 155.43) * mm, "end": v(-179.78, 155.43) * mm});
            skLineSegment(sketch, "E478.left", {"start": v(-184.45, 159.16) * mm, "end": v(-184.45, 155.43) * mm});
            skLineSegment(sketch, "E478.right", {"start": v(-179.78, 159.16) * mm, "end": v(-179.78, 155.43) * mm});
            skLineSegment(sketch, "E479.left", {"start": v(-189.24, 161.01) * mm, "end": v(-189.24, 159.07) * mm});
            skLineSegment(sketch, "E479.right", {"start": v(-187.71, 161.01) * mm, "end": v(-187.71, 159.07) * mm});
            skLineSegment(sketch, "E480.bottom", {"start": v(-190.83, 162.8) * mm, "end": v(-186.2, 162.8) * mm});
            skLineSegment(sketch, "E480.top", {"start": v(-190.83, 161.01) * mm, "end": v(-189.24, 161.01) * mm});
            skLineSegment(sketch, "E480.left", {"start": v(-190.83, 162.8) * mm, "end": v(-190.83, 161.01) * mm});
            skLineSegment(sketch, "E480.right", {"start": v(-186.2, 162.8) * mm, "end": v(-186.2, 161.01) * mm});
            skLineSegment(sketch, "E481.bottom", {"start": v(-184.47, 162.8) * mm, "end": v(-179.78, 162.8) * mm});
            skLineSegment(sketch, "E481.top", {"start": v(-184.47, 161.03) * mm, "end": v(-182.78, 161.03) * mm});
            skLineSegment(sketch, "E481.left", {"start": v(-184.47, 162.8) * mm, "end": v(-184.47, 161.03) * mm});
            skLineSegment(sketch, "E481.right", {"start": v(-179.78, 162.8) * mm, "end": v(-179.78, 161.03) * mm});
            skLineSegment(sketch, "E482.left", {"start": v(-182.78, 161.03) * mm, "end": v(-182.78, 159.16) * mm});
            skLineSegment(sketch, "E482.right", {"start": v(-181.36, 161.03) * mm, "end": v(-181.36, 159.16) * mm});
            skLineSegment(sketch, "E483.bottom", {"start": v(-195.47, 164.63) * mm, "end": v(-192.43, 164.63) * mm});
            skLineSegment(sketch, "E483.top", {"start": v(-194.01, 161.06) * mm, "end": v(-192.43, 161.06) * mm});
            skLineSegment(sketch, "E483.left", {"start": v(-195.47, 164.63) * mm, "end": v(-195.47, 162.76) * mm});
            skLineSegment(sketch, "E483.right", {"start": v(-192.43, 164.63) * mm, "end": v(-192.43, 161.06) * mm});
            skLineSegment(sketch, "E484.left", {"start": v(-195.47, 161.06) * mm, "end": v(-195.47, 159.07) * mm});
            skLineSegment(sketch, "E484.right", {"start": v(-194.01, 161.06) * mm, "end": v(-194.01, 159.07) * mm});
            skLineSegment(sketch, "E485.bottom", {"start": v(-195.47, 162.76) * mm, "end": v(-197.21, 162.76) * mm});
            skLineSegment(sketch, "E485.top", {"start": v(-195.47, 161.06) * mm, "end": v(-197.21, 161.06) * mm});
            skLineSegment(sketch, "E485.right", {"start": v(-197.21, 162.76) * mm, "end": v(-197.21, 161.06) * mm});
            skLineSegment(sketch, "E486.bottom", {"start": v(-178.2, 164.67) * mm, "end": v(-175.09, 164.67) * mm});
            skLineSegment(sketch, "E486.top", {"start": v(-178.2, 160.96) * mm, "end": v(-176.59, 160.96) * mm});
            skLineSegment(sketch, "E486.left", {"start": v(-178.2, 164.67) * mm, "end": v(-178.2, 160.96) * mm});
            skLineSegment(sketch, "E486.right", {"start": v(-175.09, 164.67) * mm, "end": v(-175.09, 162.81) * mm});
            skLineSegment(sketch, "E487.bottom", {"start": v(-175.09, 162.81) * mm, "end": v(-173.36, 162.81) * mm});
            skLineSegment(sketch, "E487.top", {"start": v(-175.09, 160.96) * mm, "end": v(-173.36, 160.96) * mm});
            skLineSegment(sketch, "E487.right", {"start": v(-173.36, 162.81) * mm, "end": v(-173.36, 160.96) * mm});
            skLineSegment(sketch, "E488.top", {"start": v(-175.09, 157.26) * mm, "end": v(-176.59, 157.26) * mm});
            skLineSegment(sketch, "E488.left", {"start": v(-175.09, 160.96) * mm, "end": v(-175.09, 157.26) * mm});
            skLineSegment(sketch, "E489.bottom", {"start": v(-176.59, 159.1) * mm, "end": v(-178.13, 159.1) * mm});
            skLineSegment(sketch, "E489.top", {"start": v(-176.59, 157.24) * mm, "end": v(-178.13, 157.24) * mm});
            skLineSegment(sketch, "E489.right", {"start": v(-178.13, 159.1) * mm, "end": v(-178.13, 157.24) * mm});
            skLineSegment(sketch, "E490.trimOffspring", {"start": v(-194.01, 159.07) * mm, "end": v(-192.45, 159.07) * mm});
            skLineSegment(sketch, "E491.trimOffspring", {"start": v(-187.71, 161.01) * mm, "end": v(-186.2, 161.01) * mm});
            skLineSegment(sketch, "E492.trimOffspring", {"start": v(-187.71, 159.2) * mm, "end": v(-186.05, 159.2) * mm});
            skLineSegment(sketch, "E493.trimOffspring", {"start": v(-181.36, 161.03) * mm, "end": v(-179.78, 161.03) * mm});
            skLineSegment(sketch, "E494.trimOffspring", {"start": v(-181.36, 159.16) * mm, "end": v(-179.78, 159.16) * mm});
            skLineSegment(sketch, "E495", {"start": v(-214.51, 127.77) * mm, "end": v(-209.84, 127.77) * mm});
            skLineSegment(sketch, "E496", {"start": v(-209.84, 127.77) * mm, "end": v(-209.84, 125.98) * mm});
            skLineSegment(sketch, "E497", {"start": v(-209.84, 125.98) * mm, "end": v(-203.52, 125.98) * mm});
            skLineSegment(sketch, "E498.bottom", {"start": v(-225.9, 129.23) * mm, "end": v(-227.44, 129.23) * mm});
            skLineSegment(sketch, "E498.top", {"start": v(-225.9, 132.16) * mm, "end": v(-227.44, 132.16) * mm});
            skLineSegment(sketch, "E498.left", {"start": v(-225.9, 129.23) * mm, "end": v(-225.9, 132.16) * mm});
            skLineSegment(sketch, "E498.right", {"start": v(-227.44, 129.23) * mm, "end": v(-227.44, 132.16) * mm});
            skLineSegment(sketch, "E499.bottom", {"start": v(-224.61, 122.94) * mm, "end": v(-225.98, 122.94) * mm});
            skLineSegment(sketch, "E499.top", {"start": v(-224.61, 121.6) * mm, "end": v(-225.98, 121.6) * mm});
            skLineSegment(sketch, "E499.left", {"start": v(-224.61, 122.94) * mm, "end": v(-224.61, 121.6) * mm});
            skLineSegment(sketch, "E499.right", {"start": v(-225.98, 122.94) * mm, "end": v(-225.98, 121.6) * mm});
            skLineSegment(sketch, "E500.bottom", {"start": v(-223.26, 121.47) * mm, "end": v(-224.61, 121.47) * mm});
            skLineSegment(sketch, "E500.top", {"start": v(-223.26, 119.95) * mm, "end": v(-224.61, 119.95) * mm});
            skLineSegment(sketch, "E500.right", {"start": v(-224.61, 121.47) * mm, "end": v(-224.61, 119.95) * mm});
            skLineSegment(sketch, "E501.top", {"start": v(-227.44, 141.16) * mm, "end": v(-226.03, 141.16) * mm});
            skLineSegment(sketch, "E501.left", {"start": v(-227.44, 142.75) * mm, "end": v(-227.44, 141.16) * mm});
            skLineSegment(sketch, "E501.right", {"start": v(-226.03, 142.75) * mm, "end": v(-226.03, 141.16) * mm});
            skLineSegment(sketch, "E502.bottom", {"start": v(-226.03, 141.16) * mm, "end": v(-224.61, 141.16) * mm});
            skLineSegment(sketch, "E502.top", {"start": v(-226.03, 139.73) * mm, "end": v(-224.61, 139.73) * mm});
            skLineSegment(sketch, "E502.left", {"start": v(-226.03, 141.16) * mm, "end": v(-226.03, 139.73) * mm});
            skLineSegment(sketch, "E502.right", {"start": v(-224.61, 141.16) * mm, "end": v(-224.61, 139.73) * mm});
            skLineSegment(sketch, "E503.bottom", {"start": v(-224.61, 141.16) * mm, "end": v(-224.61, 141.16) * mm});
            skLineSegment(sketch, "E503.top", {"start": v(-224.61, 141.03) * mm, "end": v(-224.61, 141.03) * mm});
            skLineSegment(sketch, "E503.left", {"start": v(-224.61, 141.16) * mm, "end": v(-224.61, 141.03) * mm});
            skLineSegment(sketch, "E503.right", {"start": v(-224.61, 141.16) * mm, "end": v(-224.61, 141.03) * mm});
            skLineSegment(sketch, "E504.bottom", {"start": v(-224.61, 141.16) * mm, "end": v(-223.16, 141.16) * mm});
            skLineSegment(sketch, "E504.top", {"start": v(-224.61, 142.75) * mm, "end": v(-223.16, 142.75) * mm});
            skLineSegment(sketch, "E504.left", {"start": v(-224.61, 141.16) * mm, "end": v(-224.61, 142.75) * mm});
            skLineSegment(sketch, "E504.right", {"start": v(-223.16, 141.16) * mm, "end": v(-223.16, 142.75) * mm});
            skLineSegment(sketch, "E505.bottom", {"start": v(-224.61, 142.75) * mm, "end": v(-226.03, 142.75) * mm});
            skLineSegment(sketch, "E505.top", {"start": v(-224.61, 144.1) * mm, "end": v(-226.03, 144.1) * mm});
            skLineSegment(sketch, "E505.left", {"start": v(-224.61, 142.75) * mm, "end": v(-224.61, 144.1) * mm});
            skLineSegment(sketch, "E506.bottom", {"start": v(-224.61, 145.67) * mm, "end": v(-220.31, 145.67) * mm});
            skLineSegment(sketch, "E506.top", {"start": v(-224.61, 144.25) * mm, "end": v(-220.31, 144.25) * mm});
            skLineSegment(sketch, "E506.left", {"start": v(-224.61, 145.67) * mm, "end": v(-224.61, 144.25) * mm});
            skLineSegment(sketch, "E506.right", {"start": v(-220.31, 145.67) * mm, "end": v(-220.31, 144.25) * mm});
            skLineSegment(sketch, "E507.bottom", {"start": v(-223.16, 142.75) * mm, "end": v(-221.74, 142.75) * mm});
            skLineSegment(sketch, "E507.top", {"start": v(-223.16, 144.25) * mm, "end": v(-221.74, 144.25) * mm});
            skLineSegment(sketch, "E507.left", {"start": v(-223.16, 142.75) * mm, "end": v(-223.16, 144.25) * mm});
            skLineSegment(sketch, "E507.right", {"start": v(-221.74, 142.75) * mm, "end": v(-221.74, 144.25) * mm});
            skLineSegment(sketch, "E508.bottom", {"start": v(-223.16, 141.16) * mm, "end": v(-221.7, 141.16) * mm});
            skLineSegment(sketch, "E508.top", {"start": v(-223.16, 139.73) * mm, "end": v(-221.7, 139.73) * mm});
            skLineSegment(sketch, "E508.left", {"start": v(-223.16, 141.16) * mm, "end": v(-223.16, 139.73) * mm});
            skLineSegment(sketch, "E508.right", {"start": v(-221.7, 141.16) * mm, "end": v(-221.7, 139.73) * mm});
            skLineSegment(sketch, "E509.bottom", {"start": v(-221.74, 142.75) * mm, "end": v(-220.26, 142.75) * mm});
            skLineSegment(sketch, "E509.top", {"start": v(-221.74, 141.4) * mm, "end": v(-220.26, 141.4) * mm});
            skLineSegment(sketch, "E509.left", {"start": v(-221.74, 142.75) * mm, "end": v(-221.74, 141.4) * mm});
            skLineSegment(sketch, "E509.right", {"start": v(-220.26, 142.75) * mm, "end": v(-220.26, 141.4) * mm});
            skLineSegment(sketch, "E510.bottom", {"start": v(-220.31, 144.25) * mm, "end": v(-218.88, 144.25) * mm});
            skLineSegment(sketch, "E510.top", {"start": v(-220.31, 142.65) * mm, "end": v(-218.88, 142.65) * mm});
            skLineSegment(sketch, "E510.left", {"start": v(-220.31, 144.25) * mm, "end": v(-220.31, 142.65) * mm});
            skLineSegment(sketch, "E510.right", {"start": v(-218.88, 144.25) * mm, "end": v(-218.88, 142.65) * mm});
            skLineSegment(sketch, "E511", {"start": v(-190.85, 175.67) * mm, "end": v(-187.66, 175.67) * mm});
            skLineSegment(sketch, "E512", {"start": v(-179.8, 173.81) * mm, "end": v(-178.08, 173.81) * mm});
            skSolve(sketch);
        }
        {
            var Q0;
            Q0 = qSketchRegion(id + "F0", true);
            extrude(context, id + "F1", {"entities" : qUnion([Q0]), "depth" : 4.45 * mm, "offsetDistance" : 25 * mm});
        }
    });
